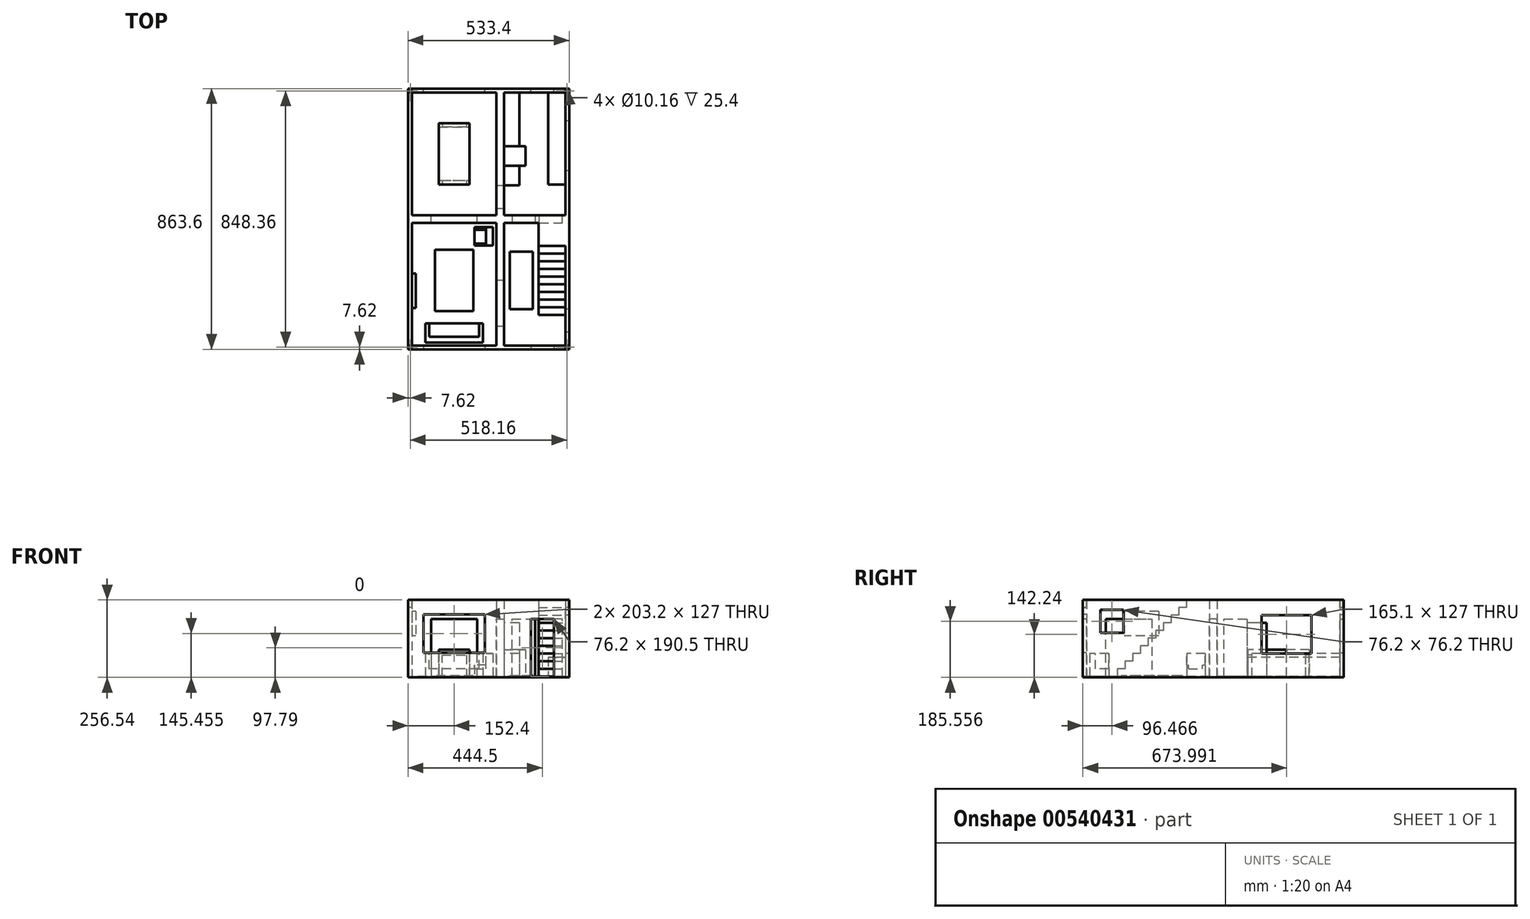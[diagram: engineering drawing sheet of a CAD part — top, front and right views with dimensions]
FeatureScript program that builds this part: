
annotation { "Feature Type Name" : "Feature", "Feature Type Description" : "" }
export const myFeature = defineFeature(function(context is Context, id is Id, definition is map)
    precondition{}
    {
        {
            var Q0;
            Q0=qCreatedBy(makeId("Top.planeOp"),FACE);
            var sketch = newSketch(context, id + "F0", { "sketchPlane" : qUnion([Q0])});
            skLineSegment(sketch, "E0.bottom", {"start": v(266.7, 431.8) * mm, "end": v(-266.7, 431.8) * mm});
            skLineSegment(sketch, "E0.top", {"start": v(266.7, -431.8) * mm, "end": v(-266.7, -431.8) * mm});
            skLineSegment(sketch, "E0.left", {"start": v(266.7, 431.8) * mm, "end": v(266.7, -431.8) * mm});
            skLineSegment(sketch, "E0.right", {"start": v(-266.7, 431.8) * mm, "end": v(-266.7, -431.8) * mm});
            skPoint(sketch, "E0.middle", {"position": v(0, 0) * mm});
            skSolve(sketch);
        }
        {
            var Q0;
            Q0=makeQuery(id+"F0.imprint","IMPRINT",FACE,{"disambiguationData":[TD([[makeQuery(id+"F0.imprint","IMPRINT",EDGE,{"derivedFrom":sQuery(id+"F0.wireOp",EDGE,"E0.bottom")}),1.0]])]});
            extrude(context, id + "F1", {"entities" : qUnion([Q0]), "depth" : 2.54 * mm, "offsetDistance" : 25.4 * mm});
        }
        {
            var Q0;
            Q0=makeQuery(id+"F1.opExtrude","CAP_FACE",FACE,{"disambiguationData":[OSD([sQuery(id+"F0.wireOp",EDGE,"E0.bottom"),sQuery(id+"F0.wireOp",EDGE,"E0.top"),sQuery(id+"F0.wireOp",EDGE,"E0.left"),sQuery(id+"F0.wireOp",EDGE,"E0.right")])],"isStart":false});
            var sketch = newSketch(context, id + "F2", { "sketchPlane" : qUnion([Q0])});
            skLineSegment(sketch, "E1.bottom", {"start": v(254, 419.1) * mm, "end": v(-254, 419.1) * mm});
            skLineSegment(sketch, "E1.top", {"start": v(254, -419.1) * mm, "end": v(-254, -419.1) * mm});
            skLineSegment(sketch, "E1.left", {"start": v(254, 419.1) * mm, "end": v(254, -419.1) * mm});
            skLineSegment(sketch, "E1.right", {"start": v(-254, 419.1) * mm, "end": v(-254, -419.1) * mm});
            skPoint(sketch, "E1.middle", {"position": v(0, 0) * mm});
            skSolve(sketch);
        }
        {
            var Q0;
            Q0=makeQuery(id+"F2.imprint","IMPRINT",FACE,{"disambiguationData":[TD([[makeQuery(id+"F2.imprint","IMPRINT",EDGE,{"derivedFrom":sQuery(id+"F2.wireOp",EDGE,"E1.bottom")}),-1.0]])]});
            extrude(context, id + "F3", {"entities" : qUnion([Q0]), "operationType" : NewBodyOperationType.ADD, "depth" : 254 * mm, "offsetDistance" : 25.4 * mm});
        }
        {
            var Q0;
            Q0=makeQuery(id+"F1.opExtrude","CAP_FACE",FACE,{"disambiguationData":[OSD([sQuery(id+"F0.wireOp",EDGE,"E0.bottom"),sQuery(id+"F0.wireOp",EDGE,"E0.top"),sQuery(id+"F0.wireOp",EDGE,"E0.left"),sQuery(id+"F0.wireOp",EDGE,"E0.right")])],"isStart":false});
            var sketch = newSketch(context, id + "F4", { "sketchPlane" : qUnion([Q0])});
            skLineSegment(sketch, "E2", {"start": v(50.8, 419.1) * mm, "end": v(50.8, -419.1) * mm});
            skLineSegment(sketch, "E3", {"start": v(50.8, 419.1) * mm, "end": v(25.4, 419.1) * mm});
            skLineSegment(sketch, "E4", {"start": v(25.4, 419.1) * mm, "end": v(25.4, -419.1) * mm});
            skLineSegment(sketch, "E5", {"start": v(25.4, -419.1) * mm, "end": v(50.8, -419.1) * mm});
            skLineSegment(sketch, "E6", {"start": v(254, -12.7) * mm, "end": v(254, 0) * mm});
            skLineSegment(sketch, "E7", {"start": v(-254, 0) * mm, "end": v(-254, -12.7) * mm});
            skLineSegment(sketch, "E8", {"start": v(254, -12.7) * mm, "end": v(-254, -12.7) * mm});
            skLineSegment(sketch, "E9", {"start": v(-254, 12.7) * mm, "end": v(254, 12.7) * mm});
            skSolve(sketch);
        }
        {
            var Q0;
            {var subQ0=sQuery(id+"F4.wireOp",EDGE,"E5");Q0=makeQuery(id+"F4.imprint","IMPRINT",FACE,{"disambiguationData":[TD([[makeQuery(id+"F4.imprint","IMPRINT",EDGE,{"derivedFrom":subQ0}),-1.0]])]});}
            var Q1;
            {var subQ0=sQuery(id+"F4.wireOp",EDGE,"E9");var subQ1=sQuery(id+"F4.wireOp",EDGE,"E2");var subQ2=makeQuery(id+"F4.imprint","INTERSECT",VERTEX,{"derivedFrom":[subQ1,subQ0]});Q1=makeQuery(id+"F4.imprint","IMPRINT",FACE,{"disambiguationData":[TD([[makeQuery(id+"F4.imprint","IMPRINT",EDGE,{"disambiguationData":[TD([[subQ2,-1.0]])],"derivedFrom":subQ1}),-1.0]])]});}
            var Q2;
            {var subQ6=sQuery(id+"F4.wireOp",EDGE,"E6");Q2=makeQuery(id+"F4.imprint","IMPRINT",FACE,{"disambiguationData":[TD([[makeQuery(id+"F4.imprint","IMPRINT",EDGE,{"derivedFrom":subQ6}),-1.0]])]});}
            var Q3;
            {var subQ6=sQuery(id+"F4.wireOp",EDGE,"E7");Q3=makeQuery(id+"F4.imprint","IMPRINT",FACE,{"disambiguationData":[TD([[makeQuery(id+"F4.imprint","IMPRINT",EDGE,{"derivedFrom":subQ6}),1.0]])]});}
            var Q4;
            {var subQ0=sQuery(id+"F4.wireOp",EDGE,"E3");Q4=makeQuery(id+"F4.imprint","IMPRINT",FACE,{"disambiguationData":[TD([[makeQuery(id+"F4.imprint","IMPRINT",EDGE,{"derivedFrom":subQ0}),1.0]])]});}
            extrude(context, id + "F5", {"entities" : qUnion([Q0, Q1, Q2, Q3, Q4]), "operationType" : NewBodyOperationType.ADD, "depth" : 254 * mm, "offsetDistance" : 25.4 * mm});
        }
        {
            var Q0;
            {var subQ0=sQuery(id+"F0.wireOp",EDGE,"E0.top");Q0=makeQuery(id+"F3.boolean.opBoolean","MERGE",FACE,{"derivedFrom":[makeQuery(id+"F1.opExtrude","SWEPT_FACE",FACE,{"disambiguationData":[OSD([subQ0])]}),makeQuery(id+"F3.opExtrude","SWEPT_FACE",FACE,{"disambiguationData":[OSD([subQ0])]})]});}
            var sketch = newSketch(context, id + "F6", { "sketchPlane" : qUnion([Q0])});
            skLineSegment(sketch, "E10", {"start": v(139.7, 193.04) * mm, "end": v(215.9, 193.04) * mm});
            skLineSegment(sketch, "E11", {"start": v(215.9, 193.04) * mm, "end": v(215.9, 2.54) * mm});
            skLineSegment(sketch, "E12", {"start": v(215.9, 2.54) * mm, "end": v(139.7, 2.54) * mm});
            skLineSegment(sketch, "E13", {"start": v(139.7, 2.54) * mm, "end": v(139.7, 193.04) * mm});
            skSolve(sketch);
        }
        {
            var Q0;
            Q0=makeQuery(id+"F6.imprint","IMPRINT",FACE,{"disambiguationData":[TD([[makeQuery(id+"F6.imprint","IMPRINT",EDGE,{"derivedFrom":sQuery(id+"F6.wireOp",EDGE,"E10")}),-1.0]])]});
            extrude(context, id + "F7", {"entities" : qUnion([Q0]), "operationType" : NewBodyOperationType.REMOVE, "oppositeDirection" : true, "depth" : 25.4 * mm, "offsetDistance" : 25.4 * mm});
        }
        {
            var Q0;
            {var subQ2=sQuery(id+"F4.wireOp",EDGE,"E8");var subQ3=sQuery(id+"F4.wireOp",EDGE,"E2");var subQ4=makeQuery(id+"F4.imprint","INTERSECT",VERTEX,{"derivedFrom":[subQ3,subQ2]});Q0=makeQuery(id+"F7.boolean.opBoolean","MERGE",FACE,{"derivedFrom":[makeQuery(id+"F5.boolean.opBoolean","SPLIT",FACE,{"disambiguationData":[TD([makeQuery(id+"F5.opExtrude","SWEPT_FACE",FACE,{"disambiguationData":[OSD([subQ3]),TDD([makeQuery(id+"F4.imprint","IMPRINT",EDGE,{"disambiguationData":[TD([[subQ4,-1.0]])],"derivedFrom":subQ3})])]})])],"derivedFrom":makeQuery(id+"F1.opExtrude","CAP_FACE",FACE,{"disambiguationData":[OSD([sQuery(id+"F0.wireOp",EDGE,"E0.bottom"),sQuery(id+"F0.wireOp",EDGE,"E0.top"),sQuery(id+"F0.wireOp",EDGE,"E0.left"),sQuery(id+"F0.wireOp",EDGE,"E0.right")])],"isStart":false})}),makeQuery(id+"F7.opExtrude","SWEPT_FACE",FACE,{"disambiguationData":[OSD([sQuery(id+"F6.wireOp",EDGE,"E12")])]})]});}
            var sketch = newSketch(context, id + "F8", { "sketchPlane" : qUnion([Q0])});
            skLineSegment(sketch, "E14", {"start": v(254, -12.7) * mm, "end": v(177.8, -12.7) * mm});
            skLineSegment(sketch, "E15", {"start": v(177.8, -12.7) * mm, "end": v(177.8, -317.5) * mm});
            skLineSegment(sketch, "E16", {"start": v(177.8, -317.5) * mm, "end": v(254, -317.5) * mm});
            skLineSegment(sketch, "E17", {"start": v(254, -12.7) * mm, "end": v(254, -317.5) * mm});
            skSolve(sketch);
        }
        {
            var Q0;
            Q0=makeQuery(id+"F8.imprint","IMPRINT",FACE,{"disambiguationData":[TD([[makeQuery(id+"F8.imprint","IMPRINT",EDGE,{"derivedFrom":sQuery(id+"F8.wireOp",EDGE,"E14")}),1.0]])]});
            extrude(context, id + "F9", {"entities" : qUnion([Q0]), "operationType" : NewBodyOperationType.ADD, "depth" : 25.4 * mm, "offsetDistance" : 25.4 * mm});
        }
        {
            var Q0;
            Q0=makeQuery(id+"F9.opExtrude","CAP_FACE",FACE,{"disambiguationData":[OSD([sQuery(id+"F8.wireOp",EDGE,"E14"),sQuery(id+"F8.wireOp",EDGE,"E15"),sQuery(id+"F8.wireOp",EDGE,"E16"),sQuery(id+"F8.wireOp",EDGE,"E17")])],"isStart":false});
            var sketch = newSketch(context, id + "F10", { "sketchPlane" : qUnion([Q0])});
            skLineSegment(sketch, "E18", {"start": v(177.8, -12.7) * mm, "end": v(177.8, -292.1) * mm});
            skLineSegment(sketch, "E19", {"start": v(177.8, -292.1) * mm, "end": v(254, -292.1) * mm});
            skLineSegment(sketch, "E20", {"start": v(254, -292.1) * mm, "end": v(254, -12.7) * mm});
            skLineSegment(sketch, "E21", {"start": v(254, -12.7) * mm, "end": v(177.8, -12.7) * mm});
            skSolve(sketch);
        }
        {
            var Q0;
            Q0 = qSketchRegion(id + "F10", true);
            extrude(context, id + "F11", {"entities" : qUnion([Q0]), "operationType" : NewBodyOperationType.ADD, "depth" : 25.4 * mm, "offsetDistance" : 25.4 * mm});
        }
        {
            var Q0;
            Q0=makeQuery(id+"F11.opExtrude","CAP_FACE",FACE,{"disambiguationData":[OSD([sQuery(id+"F10.wireOp",EDGE,"E18"),sQuery(id+"F10.wireOp",EDGE,"E19"),sQuery(id+"F10.wireOp",EDGE,"E20"),sQuery(id+"F10.wireOp",EDGE,"E21")])],"isStart":false});
            var sketch = newSketch(context, id + "F12", { "sketchPlane" : qUnion([Q0])});
            skLineSegment(sketch, "E22", {"start": v(177.8, -12.7) * mm, "end": v(177.8, -266.7) * mm});
            skLineSegment(sketch, "E23", {"start": v(177.8, -266.7) * mm, "end": v(254, -266.7) * mm});
            skLineSegment(sketch, "E24", {"start": v(254, -266.7) * mm, "end": v(254, -12.7) * mm});
            skLineSegment(sketch, "E25", {"start": v(254, -12.7) * mm, "end": v(177.8, -12.7) * mm});
            skSolve(sketch);
        }
        {
            var Q0;
            Q0 = qSketchRegion(id + "F12", true);
            extrude(context, id + "F13", {"entities" : qUnion([Q0]), "operationType" : NewBodyOperationType.ADD, "depth" : 25.4 * mm, "offsetDistance" : 25.4 * mm});
        }
        {
            var Q0;
            Q0=makeQuery(id+"F13.opExtrude","CAP_FACE",FACE,{"disambiguationData":[OSD([sQuery(id+"F12.wireOp",EDGE,"E22"),sQuery(id+"F12.wireOp",EDGE,"E23"),sQuery(id+"F12.wireOp",EDGE,"E24"),sQuery(id+"F12.wireOp",EDGE,"E25")])],"isStart":false});
            var sketch = newSketch(context, id + "F14", { "sketchPlane" : qUnion([Q0])});
            skLineSegment(sketch, "E26", {"start": v(177.8, -12.7) * mm, "end": v(177.8, -241.3) * mm});
            skLineSegment(sketch, "E27", {"start": v(177.8, -241.3) * mm, "end": v(254, -241.3) * mm});
            skLineSegment(sketch, "E28", {"start": v(254, -241.3) * mm, "end": v(254, -12.7) * mm});
            skLineSegment(sketch, "E29", {"start": v(254, -12.7) * mm, "end": v(177.8, -12.7) * mm});
            skSolve(sketch);
        }
        {
            var Q0;
            Q0 = qSketchRegion(id + "F14", true);
            extrude(context, id + "F15", {"entities" : qUnion([Q0]), "operationType" : NewBodyOperationType.ADD, "depth" : 25.4 * mm, "offsetDistance" : 25.4 * mm});
        }
        {
            var Q0;
            Q0=makeQuery(id+"F15.opExtrude","CAP_FACE",FACE,{"disambiguationData":[OSD([sQuery(id+"F14.wireOp",EDGE,"E26"),sQuery(id+"F14.wireOp",EDGE,"E27"),sQuery(id+"F14.wireOp",EDGE,"E28"),sQuery(id+"F14.wireOp",EDGE,"E29")])],"isStart":false});
            var sketch = newSketch(context, id + "F16", { "sketchPlane" : qUnion([Q0])});
            skLineSegment(sketch, "E30", {"start": v(177.8, -12.7) * mm, "end": v(177.8, -215.9) * mm});
            skLineSegment(sketch, "E31", {"start": v(177.8, -215.9) * mm, "end": v(254, -215.9) * mm});
            skLineSegment(sketch, "E32", {"start": v(254, -215.9) * mm, "end": v(254, -12.7) * mm});
            skLineSegment(sketch, "E33", {"start": v(254, -12.7) * mm, "end": v(177.8, -12.7) * mm});
            skSolve(sketch);
        }
        {
            var Q0;
            Q0 = qSketchRegion(id + "F16", true);
            extrude(context, id + "F17", {"entities" : qUnion([Q0]), "operationType" : NewBodyOperationType.ADD, "depth" : 25.4 * mm, "offsetDistance" : 25.4 * mm});
        }
        {
            var Q0;
            Q0=makeQuery(id+"F17.opExtrude","CAP_FACE",FACE,{"disambiguationData":[OSD([sQuery(id+"F16.wireOp",EDGE,"E30"),sQuery(id+"F16.wireOp",EDGE,"E31"),sQuery(id+"F16.wireOp",EDGE,"E32"),sQuery(id+"F16.wireOp",EDGE,"E33")])],"isStart":false});
            var sketch = newSketch(context, id + "F18", { "sketchPlane" : qUnion([Q0])});
            skLineSegment(sketch, "E34", {"start": v(177.8, -12.7) * mm, "end": v(177.8, -190.5) * mm});
            skLineSegment(sketch, "E35", {"start": v(177.8, -190.5) * mm, "end": v(254, -190.5) * mm});
            skLineSegment(sketch, "E36", {"start": v(254, -190.5) * mm, "end": v(254, -12.7) * mm});
            skLineSegment(sketch, "E37", {"start": v(254, -12.7) * mm, "end": v(177.8, -12.7) * mm});
            skSolve(sketch);
        }
        {
            var Q0;
            Q0 = qSketchRegion(id + "F18", true);
            extrude(context, id + "F19", {"entities" : qUnion([Q0]), "operationType" : NewBodyOperationType.ADD, "depth" : 25.4 * mm, "offsetDistance" : 25.4 * mm});
        }
        {
            var Q0;
            Q0=makeQuery(id+"F19.opExtrude","CAP_FACE",FACE,{"disambiguationData":[OSD([sQuery(id+"F18.wireOp",EDGE,"E34"),sQuery(id+"F18.wireOp",EDGE,"E35"),sQuery(id+"F18.wireOp",EDGE,"E36"),sQuery(id+"F18.wireOp",EDGE,"E37")])],"isStart":false});
            var sketch = newSketch(context, id + "F20", { "sketchPlane" : qUnion([Q0])});
            skLineSegment(sketch, "E38", {"start": v(177.8, -12.7) * mm, "end": v(177.8, -165.1) * mm});
            skLineSegment(sketch, "E39", {"start": v(177.8, -165.1) * mm, "end": v(254, -165.1) * mm});
            skLineSegment(sketch, "E40", {"start": v(254, -165.1) * mm, "end": v(254, -12.7) * mm});
            skLineSegment(sketch, "E41", {"start": v(254, -12.7) * mm, "end": v(177.8, -12.7) * mm});
            skSolve(sketch);
        }
        {
            var Q0;
            Q0 = qSketchRegion(id + "F20", true);
            extrude(context, id + "F21", {"entities" : qUnion([Q0]), "operationType" : NewBodyOperationType.ADD, "depth" : 25.4 * mm, "offsetDistance" : 25.4 * mm});
        }
        {
            var Q0;
            Q0=makeQuery(id+"F21.opExtrude","CAP_FACE",FACE,{"disambiguationData":[OSD([sQuery(id+"F20.wireOp",EDGE,"E38"),sQuery(id+"F20.wireOp",EDGE,"E39"),sQuery(id+"F20.wireOp",EDGE,"E40"),sQuery(id+"F20.wireOp",EDGE,"E41")])],"isStart":false});
            var sketch = newSketch(context, id + "F22", { "sketchPlane" : qUnion([Q0])});
            skLineSegment(sketch, "E42", {"start": v(177.8, -12.7) * mm, "end": v(177.8, -139.7) * mm});
            skLineSegment(sketch, "E43", {"start": v(177.8, -139.7) * mm, "end": v(254, -139.7) * mm});
            skLineSegment(sketch, "E44", {"start": v(254, -139.7) * mm, "end": v(254, -12.7) * mm});
            skLineSegment(sketch, "E45", {"start": v(254, -12.7) * mm, "end": v(177.8, -12.7) * mm});
            skSolve(sketch);
        }
        {
            var Q0;
            Q0=makeQuery(id+"F22.imprint","IMPRINT",FACE,{"disambiguationData":[TD([[makeQuery(id+"F22.imprint","IMPRINT",EDGE,{"derivedFrom":sQuery(id+"F22.wireOp",EDGE,"E42")}),1.0]])]});
            extrude(context, id + "F23", {"entities" : qUnion([Q0]), "operationType" : NewBodyOperationType.ADD, "depth" : 25.4 * mm, "offsetDistance" : 25.4 * mm});
        }
        {
            var Q0;
            Q0=makeQuery(id+"F23.opExtrude","CAP_FACE",FACE,{"disambiguationData":[OSD([sQuery(id+"F22.wireOp",EDGE,"E42"),sQuery(id+"F22.wireOp",EDGE,"E43"),sQuery(id+"F22.wireOp",EDGE,"E44"),sQuery(id+"F22.wireOp",EDGE,"E45")])],"isStart":false});
            var sketch = newSketch(context, id + "F24", { "sketchPlane" : qUnion([Q0])});
            skLineSegment(sketch, "E46", {"start": v(177.8, -12.7) * mm, "end": v(177.8, -114.3) * mm});
            skLineSegment(sketch, "E47", {"start": v(177.8, -114.3) * mm, "end": v(254, -114.3) * mm});
            skLineSegment(sketch, "E48", {"start": v(254, -114.3) * mm, "end": v(254, -12.7) * mm});
            skLineSegment(sketch, "E49", {"start": v(254, -12.7) * mm, "end": v(177.8, -12.7) * mm});
            skSolve(sketch);
        }
        {
            var Q0;
            Q0 = qSketchRegion(id + "F24", true);
            extrude(context, id + "F25", {"entities" : qUnion([Q0]), "operationType" : NewBodyOperationType.ADD, "depth" : 25.4 * mm, "offsetDistance" : 25.4 * mm});
        }
        {
            var Q0;
            Q0=makeQuery(id+"F25.opExtrude","CAP_FACE",FACE,{"disambiguationData":[OSD([sQuery(id+"F24.wireOp",EDGE,"E46"),sQuery(id+"F24.wireOp",EDGE,"E47"),sQuery(id+"F24.wireOp",EDGE,"E48"),sQuery(id+"F24.wireOp",EDGE,"E49")])],"isStart":false});
            var sketch = newSketch(context, id + "F26", { "sketchPlane" : qUnion([Q0])});
            skLineSegment(sketch, "E50", {"start": v(177.8, -12.7) * mm, "end": v(177.8, -88.9) * mm});
            skLineSegment(sketch, "E51", {"start": v(177.8, -88.9) * mm, "end": v(254, -88.9) * mm});
            skLineSegment(sketch, "E52", {"start": v(254, -88.9) * mm, "end": v(254, -12.7) * mm});
            skLineSegment(sketch, "E53", {"start": v(254, -12.7) * mm, "end": v(177.8, -12.7) * mm});
            skSolve(sketch);
        }
        {
            var Q0;
            Q0 = qSketchRegion(id + "F26", true);
            extrude(context, id + "F27", {"entities" : qUnion([Q0]), "operationType" : NewBodyOperationType.ADD, "depth" : 25.4 * mm, "offsetDistance" : 25.4 * mm});
        }
        {
            var Q0;
            {var subQ0=sQuery(id+"F4.wireOp",EDGE,"E8");Q0=makeQuery(id+"F5.opExtrude","SWEPT_FACE",FACE,{"disambiguationData":[OSD([subQ0]),TDD([makeQuery(id+"F4.imprint","IMPRINT",EDGE,{"disambiguationData":[TD([[makeQuery(id+"F4.imprint","INTERSECT",VERTEX,{"derivedFrom":[sQuery(id+"F4.wireOp",EDGE,"E2"),subQ0]}),1.0]])],"derivedFrom":subQ0})])]});}
            var sketch = newSketch(context, id + "F28", { "sketchPlane" : qUnion([Q0])});
            skLineSegment(sketch, "E54", {"start": v(77.55, 2.54) * mm, "end": v(77.55, 193.04) * mm});
            skLineSegment(sketch, "E55", {"start": v(77.55, 193.04) * mm, "end": v(153.75, 193.04) * mm});
            skLineSegment(sketch, "E56", {"start": v(153.75, 193.04) * mm, "end": v(153.75, 2.54) * mm});
            skLineSegment(sketch, "E57", {"start": v(153.75, 2.54) * mm, "end": v(77.55, 2.54) * mm});
            skSolve(sketch);
        }
        {
            var Q0;
            Q0=makeQuery(id+"F28.imprint","IMPRINT",FACE,{"disambiguationData":[TD([[makeQuery(id+"F28.imprint","IMPRINT",EDGE,{"derivedFrom":sQuery(id+"F28.wireOp",EDGE,"E54")}),-1.0]])]});
            extrude(context, id + "F29", {"entities" : qUnion([Q0]), "operationType" : NewBodyOperationType.REMOVE, "oppositeDirection" : true, "depth" : 25.4 * mm, "offsetDistance" : 25.4 * mm});
        }
        {
            var Q0;
            {var subQ0=sQuery(id+"F4.wireOp",EDGE,"E2");Q0=makeQuery(id+"F5.opExtrude","SWEPT_FACE",FACE,{"disambiguationData":[OSD([subQ0]),TDD([makeQuery(id+"F4.imprint","IMPRINT",EDGE,{"disambiguationData":[TD([[makeQuery(id+"F4.imprint","INTERSECT",VERTEX,{"derivedFrom":[subQ0,sQuery(id+"F4.wireOp",EDGE,"E9")]}),1.0]])],"derivedFrom":subQ0})])]});}
            var sketch = newSketch(context, id + "F30", { "sketchPlane" : qUnion([Q0])});
            skLineSegment(sketch, "E58", {"start": v(34.8, 2.54) * mm, "end": v(34.8, 193.04) * mm});
            skLineSegment(sketch, "E59", {"start": v(34.8, 193.04) * mm, "end": v(111, 193.04) * mm});
            skLineSegment(sketch, "E60", {"start": v(111, 193.04) * mm, "end": v(111, 2.54) * mm});
            skLineSegment(sketch, "E61", {"start": v(111, 2.54) * mm, "end": v(34.8, 2.54) * mm});
            skSolve(sketch);
        }
        {
            var Q0;
            Q0 = qSketchRegion(id + "F30", true);
            extrude(context, id + "F31", {"entities" : qUnion([Q0]), "operationType" : NewBodyOperationType.REMOVE, "oppositeDirection" : true, "depth" : 25.4 * mm, "offsetDistance" : 25.4 * mm});
        }
        {
            var Q0;
            {var subQ0=sQuery(id+"F4.wireOp",EDGE,"E9");Q0=makeQuery(id+"F5.opExtrude","SWEPT_FACE",FACE,{"disambiguationData":[OSD([subQ0]),TDD([makeQuery(id+"F4.imprint","IMPRINT",EDGE,{"disambiguationData":[TD([[makeQuery(id+"F4.imprint","INTERSECT",VERTEX,{"derivedFrom":[makeQuery(id+"F3.opExtrude","CAP_EDGE",EDGE,{"disambiguationData":[OSD([sQuery(id+"F2.wireOp",EDGE,"E1.right")])],"isStart":true}),subQ0]}),-1.0]])],"derivedFrom":subQ0})])]});}
            var sketch = newSketch(context, id + "F32", { "sketchPlane" : qUnion([Q0])});
            skLineSegment(sketch, "E62", {"start": v(38.1, 2.54) * mm, "end": v(38.1, 193.04) * mm});
            skLineSegment(sketch, "E63", {"start": v(38.1, 193.04) * mm, "end": v(190.5, 193.04) * mm});
            skLineSegment(sketch, "E64", {"start": v(190.5, 193.04) * mm, "end": v(190.5, 2.54) * mm});
            skLineSegment(sketch, "E65", {"start": v(190.5, 2.54) * mm, "end": v(38.1, 2.54) * mm});
            skSolve(sketch);
        }
        {
            var Q0;
            Q0 = qSketchRegion(id + "F32", true);
            extrude(context, id + "F33", {"entities" : qUnion([Q0]), "operationType" : NewBodyOperationType.REMOVE, "oppositeDirection" : true, "depth" : 25.4 * mm, "offsetDistance" : 25.4 * mm});
        }
        {
            var Q0;
            {var subQ0=sQuery(id+"F4.wireOp",EDGE,"E4");Q0=makeQuery(id+"F5.opExtrude","SWEPT_FACE",FACE,{"disambiguationData":[OSD([subQ0]),TDD([makeQuery(id+"F4.imprint","IMPRINT",EDGE,{"disambiguationData":[TD([[makeQuery(id+"F4.imprint","INTERSECT",VERTEX,{"derivedFrom":[subQ0,sQuery(id+"F4.wireOp",EDGE,"E8")]}),-1.0]])],"derivedFrom":subQ0})])]});}
            var sketch = newSketch(context, id + "F34", { "sketchPlane" : qUnion([Q0])});
            skLineSegment(sketch, "E66", {"start": v(355.6, 2.54) * mm, "end": v(355.6, 193.04) * mm});
            skLineSegment(sketch, "E67", {"start": v(355.6, 193.04) * mm, "end": v(203.2, 193.04) * mm});
            skLineSegment(sketch, "E68", {"start": v(203.2, 193.04) * mm, "end": v(203.2, 2.54) * mm});
            skPoint(sketch, "E68.endSnap0", {"position": v(215.9, 2.54) * mm});
            skLineSegment(sketch, "E69", {"start": v(203.2, 2.54) * mm, "end": v(355.6, 2.54) * mm});
            skSolve(sketch);
        }
        {
            var Q0;
            Q0 = qSketchRegion(id + "F34", true);
            extrude(context, id + "F35", {"entities" : qUnion([Q0]), "operationType" : NewBodyOperationType.REMOVE, "oppositeDirection" : true, "depth" : 25.4 * mm, "offsetDistance" : 25.4 * mm});
        }
        {
            var Q0;
            {var subQ0=sQuery(id+"F2.wireOp",EDGE,"E1.right");var subQ1=sQuery(id+"F2.wireOp",EDGE,"E1.left");Q0=makeQuery(id+"F27.boolean.opBoolean","MERGE",FACE,{"derivedFrom":[makeQuery(id+"F5.boolean.opBoolean","MERGE",FACE,{"derivedFrom":[makeQuery(id+"F3.opExtrude","CAP_FACE",FACE,{"disambiguationData":[OSD([sQuery(id+"F0.wireOp",EDGE,"E0.bottom"),sQuery(id+"F0.wireOp",EDGE,"E0.top"),sQuery(id+"F0.wireOp",EDGE,"E0.left"),sQuery(id+"F0.wireOp",EDGE,"E0.right"),sQuery(id+"F2.wireOp",EDGE,"E1.bottom"),sQuery(id+"F2.wireOp",EDGE,"E1.top"),subQ1,subQ0])],"isStart":false}),makeQuery(id+"F5.opExtrude","CAP_FACE",FACE,{"disambiguationData":[OSD([subQ1,subQ0,sQuery(id+"F4.wireOp",EDGE,"E2"),sQuery(id+"F4.wireOp",EDGE,"E3"),sQuery(id+"F4.wireOp",EDGE,"E4"),sQuery(id+"F4.wireOp",EDGE,"E5"),sQuery(id+"F4.wireOp",EDGE,"E6"),sQuery(id+"F4.wireOp",EDGE,"E7"),sQuery(id+"F4.wireOp",EDGE,"E8"),sQuery(id+"F4.wireOp",EDGE,"E9")])],"isStart":false})]}),makeQuery(id+"F27.opExtrude","CAP_FACE",FACE,{"disambiguationData":[OSD([sQuery(id+"F26.wireOp",EDGE,"E50"),sQuery(id+"F26.wireOp",EDGE,"E51"),sQuery(id+"F26.wireOp",EDGE,"E52"),sQuery(id+"F26.wireOp",EDGE,"E53")])],"isStart":false})]});}
            var sketch = newSketch(context, id + "F36", { "sketchPlane" : qUnion([Q0])});
            skLineSegment(sketch, "E70.0", {"start": v(177.8, -88.9) * mm, "end": v(254, -88.9) * mm});
            skLineSegment(sketch, "E71.0", {"start": v(254, -419.1) * mm, "end": v(50.8, -419.1) * mm});
            skLineSegment(sketch, "E72", {"start": v(177.8, -88.9) * mm, "end": v(177.8, -12.7) * mm});
            skLineSegment(sketch, "E73", {"start": v(254, -12.7) * mm, "end": v(254, -88.9) * mm});
            skLineSegment(sketch, "E74", {"start": v(177.8, -12.7) * mm, "end": v(254, -12.7) * mm});
            skSolve(sketch);
        }
        {
            var Q0;
            {var subQ0=sQuery(id+"F0.wireOp",EDGE,"E0.left");Q0=makeQuery(id+"F3.boolean.opBoolean","MERGE",FACE,{"derivedFrom":[makeQuery(id+"F1.opExtrude","SWEPT_FACE",FACE,{"disambiguationData":[OSD([subQ0])]}),makeQuery(id+"F3.opExtrude","SWEPT_FACE",FACE,{"disambiguationData":[OSD([subQ0])]})]});}
            var sketch = newSketch(context, id + "F37", { "sketchPlane" : qUnion([Q0])});
            skLineSegment(sketch, "E75", {"start": v(-373.43, 223.66) * mm, "end": v(-373.43, 147.46) * mm});
            skLineSegment(sketch, "E76", {"start": v(-373.43, 147.46) * mm, "end": v(-297.23, 147.46) * mm});
            skLineSegment(sketch, "E77", {"start": v(-297.23, 147.46) * mm, "end": v(-297.23, 223.66) * mm});
            skLineSegment(sketch, "E78", {"start": v(-297.23, 223.66) * mm, "end": v(-373.43, 223.66) * mm});
            skSolve(sketch);
        }
        {
            var Q0;
            Q0=makeQuery(id+"F37.imprint","IMPRINT",FACE,{"disambiguationData":[TD([[makeQuery(id+"F37.imprint","IMPRINT",EDGE,{"derivedFrom":sQuery(id+"F37.wireOp",EDGE,"E75")}),1.0]])]});
            extrude(context, id + "F38", {"entities" : qUnion([Q0]), "operationType" : NewBodyOperationType.REMOVE, "oppositeDirection" : true, "depth" : 25.4 * mm, "offsetDistance" : 25.4 * mm});
        }
        {
            var Q0;
            {var subQ0=sQuery(id+"F0.wireOp",EDGE,"E0.top");Q0=makeQuery(id+"F3.boolean.opBoolean","MERGE",FACE,{"derivedFrom":[makeQuery(id+"F1.opExtrude","SWEPT_FACE",FACE,{"disambiguationData":[OSD([subQ0])]}),makeQuery(id+"F3.opExtrude","SWEPT_FACE",FACE,{"disambiguationData":[OSD([subQ0])]})]});}
            var sketch = newSketch(context, id + "F39", { "sketchPlane" : qUnion([Q0])});
            skLineSegment(sketch, "E79", {"start": v(-12.7, 81.95) * mm, "end": v(-215.9, 81.95) * mm});
            skLineSegment(sketch, "E80", {"start": v(-215.9, 81.95) * mm, "end": v(-215.9, 208.95) * mm});
            skLineSegment(sketch, "E81", {"start": v(-215.9, 208.95) * mm, "end": v(-12.7, 208.95) * mm});
            skLineSegment(sketch, "E82", {"start": v(-12.7, 208.95) * mm, "end": v(-12.7, 81.95) * mm});
            skSolve(sketch);
        }
        {
            var Q0;
            Q0=makeQuery(id+"F39.imprint","IMPRINT",FACE,{"disambiguationData":[TD([[makeQuery(id+"F39.imprint","IMPRINT",EDGE,{"derivedFrom":sQuery(id+"F39.wireOp",EDGE,"E79")}),-1.0]])]});
            extrude(context, id + "F40", {"entities" : qUnion([Q0]), "operationType" : NewBodyOperationType.REMOVE, "oppositeDirection" : true, "depth" : 25.4 * mm, "offsetDistance" : 25.4 * mm});
        }
        {
            var Q0;
            {var subQ0=sQuery(id+"F0.wireOp",EDGE,"E0.bottom");Q0=makeQuery(id+"F3.boolean.opBoolean","MERGE",FACE,{"derivedFrom":[makeQuery(id+"F1.opExtrude","SWEPT_FACE",FACE,{"disambiguationData":[OSD([subQ0])]}),makeQuery(id+"F3.opExtrude","SWEPT_FACE",FACE,{"disambiguationData":[OSD([subQ0])]})]});}
            var sketch = newSketch(context, id + "F41", { "sketchPlane" : qUnion([Q0])});
            skLineSegment(sketch, "E83.0", {"start": v(215.9, 208.95) * mm, "end": v(12.7, 208.95) * mm});
            skLineSegment(sketch, "E83.1", {"start": v(215.9, 81.95) * mm, "end": v(215.9, 208.95) * mm});
            skLineSegment(sketch, "E83.2", {"start": v(12.7, 81.95) * mm, "end": v(215.9, 81.95) * mm});
            skLineSegment(sketch, "E83.3", {"start": v(12.7, 208.95) * mm, "end": v(12.7, 81.95) * mm});
            skSolve(sketch);
        }
        {
            var Q0;
            Q0 = qSketchRegion(id + "F41", true);
            extrude(context, id + "F42", {"entities" : qUnion([Q0]), "operationType" : NewBodyOperationType.REMOVE, "oppositeDirection" : true, "depth" : 25.4 * mm, "offsetDistance" : 25.4 * mm});
        }
        {
            var Q0;
            {var subQ0=sQuery(id+"F0.wireOp",EDGE,"E0.bottom");Q0=makeQuery(id+"F3.boolean.opBoolean","MERGE",FACE,{"derivedFrom":[makeQuery(id+"F1.opExtrude","SWEPT_FACE",FACE,{"disambiguationData":[OSD([subQ0])]}),makeQuery(id+"F3.opExtrude","SWEPT_FACE",FACE,{"disambiguationData":[OSD([subQ0])]})]});}
            var sketch = newSketch(context, id + "F43", { "sketchPlane" : qUnion([Q0])});
            skLineSegment(sketch, "E84.0", {"start": v(-215.9, 193.04) * mm, "end": v(-215.9, 2.54) * mm});
            skLineSegment(sketch, "E85.0", {"start": v(-139.7, 193.04) * mm, "end": v(-215.9, 193.04) * mm});
            skLineSegment(sketch, "E86.0", {"start": v(-139.7, 2.54) * mm, "end": v(-139.7, 193.04) * mm});
            skLineSegment(sketch, "E87.0", {"start": v(-215.9, 2.54) * mm, "end": v(-139.7, 2.54) * mm});
            skSolve(sketch);
        }
        {
            var Q0;
            Q0=makeQuery(id+"F43.imprint","IMPRINT",FACE,{"disambiguationData":[TD([[makeQuery(id+"F43.imprint","IMPRINT",EDGE,{"derivedFrom":sQuery(id+"F43.wireOp",EDGE,"E84.0")}),1.0]])]});
            extrude(context, id + "F44", {"entities" : qUnion([Q0]), "operationType" : NewBodyOperationType.REMOVE, "oppositeDirection" : true, "depth" : 25.4 * mm, "offsetDistance" : 25.4 * mm});
        }
        {
            var Q0;
            {var subQ0=sQuery(id+"F4.wireOp",EDGE,"E9");Q0=makeQuery(id+"F5.opExtrude","SWEPT_FACE",FACE,{"disambiguationData":[OSD([subQ0]),TDD([makeQuery(id+"F4.imprint","IMPRINT",EDGE,{"disambiguationData":[TD([[makeQuery(id+"F4.imprint","INTERSECT",VERTEX,{"derivedFrom":[makeQuery(id+"F3.opExtrude","CAP_EDGE",EDGE,{"disambiguationData":[OSD([sQuery(id+"F2.wireOp",EDGE,"E1.left")])],"isStart":true}),subQ0]}),1.0]])],"derivedFrom":subQ0})])]});}
            var sketch = newSketch(context, id + "F45", { "sketchPlane" : qUnion([Q0])});
            skLineSegment(sketch, "E88", {"start": v(-244.8, 2.54) * mm, "end": v(-244.8, 193.04) * mm});
            skLineSegment(sketch, "E89", {"start": v(-244.8, 193.04) * mm, "end": v(-168.6, 193.04) * mm});
            skLineSegment(sketch, "E90", {"start": v(-168.6, 193.04) * mm, "end": v(-168.6, 2.54) * mm});
            skLineSegment(sketch, "E91", {"start": v(-168.6, 2.54) * mm, "end": v(-244.8, 2.54) * mm});
            skSolve(sketch);
        }
        {
            var Q0;
            Q0 = qSketchRegion(id + "F45", true);
            extrude(context, id + "F46", {"entities" : qUnion([Q0]), "operationType" : NewBodyOperationType.REMOVE, "oppositeDirection" : true, "depth" : 25.4 * mm, "offsetDistance" : 25.4 * mm});
        }
        {
            var Q0;
            Q0=makeQuery(id+"F27.boolean.opBoolean","MERGE",FACE,{"derivedFrom":[makeQuery(id+"F25.boolean.opBoolean","MERGE",FACE,{"derivedFrom":[makeQuery(id+"F23.boolean.opBoolean","MERGE",FACE,{"derivedFrom":[makeQuery(id+"F21.boolean.opBoolean","MERGE",FACE,{"derivedFrom":[makeQuery(id+"F19.boolean.opBoolean","MERGE",FACE,{"derivedFrom":[makeQuery(id+"F17.boolean.opBoolean","MERGE",FACE,{"derivedFrom":[makeQuery(id+"F15.boolean.opBoolean","MERGE",FACE,{"derivedFrom":[makeQuery(id+"F13.boolean.opBoolean","MERGE",FACE,{"derivedFrom":[makeQuery(id+"F11.boolean.opBoolean","MERGE",FACE,{"derivedFrom":[makeQuery(id+"F9.opExtrude","SWEPT_FACE",FACE,{"disambiguationData":[OSD([sQuery(id+"F8.wireOp",EDGE,"E15")])]}),makeQuery(id+"F11.opExtrude","SWEPT_FACE",FACE,{"disambiguationData":[OSD([sQuery(id+"F10.wireOp",EDGE,"E18")])]})]}),makeQuery(id+"F13.opExtrude","SWEPT_FACE",FACE,{"disambiguationData":[OSD([sQuery(id+"F12.wireOp",EDGE,"E22")])]})]}),makeQuery(id+"F15.opExtrude","SWEPT_FACE",FACE,{"disambiguationData":[OSD([sQuery(id+"F14.wireOp",EDGE,"E26")])]})]}),makeQuery(id+"F17.opExtrude","SWEPT_FACE",FACE,{"disambiguationData":[OSD([sQuery(id+"F16.wireOp",EDGE,"E30")])]})]}),makeQuery(id+"F19.opExtrude","SWEPT_FACE",FACE,{"disambiguationData":[OSD([sQuery(id+"F18.wireOp",EDGE,"E34")])]})]}),makeQuery(id+"F21.opExtrude","SWEPT_FACE",FACE,{"disambiguationData":[OSD([sQuery(id+"F20.wireOp",EDGE,"E38")])]})]}),makeQuery(id+"F23.opExtrude","SWEPT_FACE",FACE,{"disambiguationData":[OSD([sQuery(id+"F22.wireOp",EDGE,"E42")])]})]}),makeQuery(id+"F25.opExtrude","SWEPT_FACE",FACE,{"disambiguationData":[OSD([sQuery(id+"F24.wireOp",EDGE,"E46")])]})]}),makeQuery(id+"F27.opExtrude","SWEPT_FACE",FACE,{"disambiguationData":[OSD([sQuery(id+"F26.wireOp",EDGE,"E50")])]})]});
            var sketch = newSketch(context, id + "F47", { "sketchPlane" : qUnion([Q0])});
            skLineSegment(sketch, "E92.0", {"start": v(88.9, 256.54) * mm, "end": v(12.7, 256.54) * mm});
            skLineSegment(sketch, "E93.0", {"start": v(88.9, 256.54) * mm, "end": v(88.9, 231.14) * mm});
            skLineSegment(sketch, "E94.0", {"start": v(88.9, 231.14) * mm, "end": v(114.3, 231.14) * mm});
            skLineSegment(sketch, "E95.0", {"start": v(114.3, 231.14) * mm, "end": v(114.3, 205.74) * mm});
            skLineSegment(sketch, "E96.0", {"start": v(114.3, 205.74) * mm, "end": v(139.7, 205.74) * mm});
            skLineSegment(sketch, "E97.0", {"start": v(139.7, 205.74) * mm, "end": v(139.7, 180.34) * mm});
            skLineSegment(sketch, "E98.0", {"start": v(139.7, 180.34) * mm, "end": v(165.1, 180.34) * mm});
            skLineSegment(sketch, "E99.0", {"start": v(165.1, 180.34) * mm, "end": v(165.1, 154.94) * mm});
            skLineSegment(sketch, "E100.0", {"start": v(165.1, 154.94) * mm, "end": v(190.5, 154.94) * mm});
            skLineSegment(sketch, "E101.0", {"start": v(190.5, 154.94) * mm, "end": v(190.5, 129.54) * mm});
            skLineSegment(sketch, "E102.0", {"start": v(190.5, 129.54) * mm, "end": v(215.9, 129.54) * mm});
            skLineSegment(sketch, "E103.0", {"start": v(215.9, 129.54) * mm, "end": v(215.9, 104.14) * mm});
            skLineSegment(sketch, "E104.0", {"start": v(215.9, 104.14) * mm, "end": v(241.3, 104.14) * mm});
            skLineSegment(sketch, "E105.0", {"start": v(241.3, 104.14) * mm, "end": v(241.3, 78.74) * mm});
            skLineSegment(sketch, "E106.0", {"start": v(241.3, 78.74) * mm, "end": v(266.7, 78.74) * mm});
            skLineSegment(sketch, "E107.0", {"start": v(266.7, 78.74) * mm, "end": v(266.7, 53.34) * mm});
            skLineSegment(sketch, "E108.0", {"start": v(266.7, 53.34) * mm, "end": v(292.1, 53.34) * mm});
            skLineSegment(sketch, "E109.0", {"start": v(292.1, 53.34) * mm, "end": v(292.1, 27.94) * mm});
            skLineSegment(sketch, "E110.0", {"start": v(292.1, 27.94) * mm, "end": v(317.5, 27.94) * mm});
            skLineSegment(sketch, "E111.0", {"start": v(317.5, 27.94) * mm, "end": v(317.5, 2.54) * mm});
            skLineSegment(sketch, "E112.0", {"start": v(12.7, 2.54) * mm, "end": v(317.5, 2.54) * mm});
            skLineSegment(sketch, "E113.0", {"start": v(12.7, 193.04) * mm, "end": v(12.7, 2.54) * mm});
            skLineSegment(sketch, "E114.0", {"start": v(12.7, 256.54) * mm, "end": v(12.7, 193.04) * mm});
            skSolve(sketch);
        }
        {
            var Q0;
            Q0 = qSketchRegion(id + "F47", true);
            extrude(context, id + "F48", {"entities" : qUnion([Q0]), "operationType" : NewBodyOperationType.ADD, "depth" : 12.7 * mm, "offsetDistance" : 25.4 * mm});
        }
        {
            var Q0;
            {var subQ3=sQuery(id+"F2.wireOp",EDGE,"E1.left");var subQ4=sQuery(id+"F2.wireOp",EDGE,"E1.bottom");Q0=makeQuery(id+"F5.boolean.opBoolean","SPLIT",FACE,{"disambiguationData":[TD([makeQuery(id+"F3.opExtrude","SWEPT_FACE",FACE,{"disambiguationData":[OSD([subQ4])]})])],"derivedFrom":makeQuery(id+"F3.opExtrude","SWEPT_FACE",FACE,{"disambiguationData":[OSD([subQ3])]})});}
            var sketch = newSketch(context, id + "F49", { "sketchPlane" : qUnion([Q0])});
            skLineSegment(sketch, "E115", {"start": v(-324.74, 205.74) * mm, "end": v(-324.74, 78.74) * mm});
            skLineSegment(sketch, "E116", {"start": v(-324.74, 78.74) * mm, "end": v(-159.64, 78.74) * mm});
            skLineSegment(sketch, "E117", {"start": v(-159.64, 78.74) * mm, "end": v(-159.64, 205.74) * mm});
            skLineSegment(sketch, "E118", {"start": v(-159.64, 205.74) * mm, "end": v(-324.74, 205.74) * mm});
            skLineSegment(sketch, "E119.0", {"start": v(-419.1, 2.54) * mm, "end": v(-12.7, 2.54) * mm});
            skSolve(sketch);
        }
        {
            var Q0;
            Q0 = qSketchRegion(id + "F49", true);
            extrude(context, id + "F50", {"entities" : qUnion([Q0]), "operationType" : NewBodyOperationType.REMOVE, "oppositeDirection" : true, "depth" : 25.4 * mm, "offsetDistance" : 25.4 * mm});
        }
        {
            var Q0;
            Q0=makeQuery(id+"F36.imprint","IMPRINT",FACE,{"disambiguationData":[TD([[makeQuery(id+"F36.imprint","IMPRINT",EDGE,{"derivedFrom":sQuery(id+"F36.wireOp",EDGE,"E71.0")}),1.0]])]});
            var sketch = newSketch(context, id + "F51", { "sketchPlane" : qUnion([Q0])});
            skCircle(sketch, "E120", {"center": v(259.08, -424.18) * mm, "radius": 5.08 * mm});
            skCircle(sketch, "E121", {"center": v(-259.08, -424.18) * mm, "radius": 5.08 * mm});
            skCircle(sketch, "E122", {"center": v(-259.08, 424.18) * mm, "radius": 5.08 * mm});
            skCircle(sketch, "E123", {"center": v(259.08, 424.18) * mm, "radius": 5.08 * mm});
            skSolve(sketch);
        }
        {
            var Q0;
            Q0 = qSketchRegion(id + "F51", true);
            extrude(context, id + "F52", {"entities" : qUnion([Q0]), "operationType" : NewBodyOperationType.REMOVE, "oppositeDirection" : true, "depth" : 25.4 * mm, "offsetDistance" : 25.4 * mm});
        }
        {
            var Q0;
            {var subQ2=sQuery(id+"F2.wireOp",EDGE,"E1.left");var subQ4=sQuery(id+"F4.wireOp",EDGE,"E8");var subQ5=makeQuery(id+"F3.opExtrude","CAP_EDGE",EDGE,{"disambiguationData":[OSD([subQ2])],"isStart":true});var subQ6=sQuery(id+"F4.wireOp",EDGE,"E2");var subQ7=makeQuery(id+"F4.imprint","INTERSECT",VERTEX,{"derivedFrom":[subQ6,subQ4]});var subQ10=makeQuery(id+"F1.opExtrude","CAP_FACE",FACE,{"disambiguationData":[OSD([sQuery(id+"F0.wireOp",EDGE,"E0.bottom"),sQuery(id+"F0.wireOp",EDGE,"E0.top"),sQuery(id+"F0.wireOp",EDGE,"E0.left"),sQuery(id+"F0.wireOp",EDGE,"E0.right")])],"isStart":false});var subQ15=sQuery(id+"F4.wireOp",EDGE,"E9");var subQ17=sQuery(id+"F2.wireOp",EDGE,"E1.right");var subQ19=sQuery(id+"F4.wireOp",EDGE,"E4");var subQ21=makeQuery(id+"F3.opExtrude","CAP_EDGE",EDGE,{"disambiguationData":[OSD([subQ17])],"isStart":true});var subQ22=makeQuery(id+"F4.imprint","INTERSECT",VERTEX,{"derivedFrom":[subQ19,subQ4]});Q0=makeQuery(id+"F46.boolean.opBoolean","MERGE",FACE,{"derivedFrom":[makeQuery(id+"F44.boolean.opBoolean","MERGE",FACE,{"derivedFrom":[makeQuery(id+"F35.boolean.opBoolean","MERGE",FACE,{"derivedFrom":[makeQuery(id+"F33.boolean.opBoolean","MERGE",FACE,{"derivedFrom":[makeQuery(id+"F5.boolean.opBoolean","SPLIT",FACE,{"disambiguationData":[TD([makeQuery(id+"F5.opExtrude","SWEPT_FACE",FACE,{"disambiguationData":[OSD([subQ19]),TDD([makeQuery(id+"F4.imprint","IMPRINT",EDGE,{"disambiguationData":[TD([[subQ22,-1.0]])],"derivedFrom":subQ19})])]})])],"derivedFrom":subQ10}),makeQuery(id+"F31.boolean.opBoolean","MERGE",FACE,{"derivedFrom":[makeQuery(id+"F5.boolean.opBoolean","SPLIT",FACE,{"disambiguationData":[TD([makeQuery(id+"F5.opExtrude","SWEPT_FACE",FACE,{"disambiguationData":[OSD([subQ15]),TDD([makeQuery(id+"F4.imprint","IMPRINT",EDGE,{"disambiguationData":[TD([[makeQuery(id+"F4.imprint","INTERSECT",VERTEX,{"derivedFrom":[subQ21,subQ15]}),-1.0]])],"derivedFrom":subQ15})])]})])],"derivedFrom":subQ10}),makeQuery(id+"F29.boolean.opBoolean","MERGE",FACE,{"derivedFrom":[makeQuery(id+"F5.boolean.opBoolean","SPLIT",FACE,{"disambiguationData":[TD([makeQuery(id+"F5.opExtrude","SWEPT_FACE",FACE,{"disambiguationData":[OSD([subQ15]),TDD([makeQuery(id+"F4.imprint","IMPRINT",EDGE,{"disambiguationData":[TD([[makeQuery(id+"F4.imprint","INTERSECT",VERTEX,{"derivedFrom":[subQ5,subQ15]}),1.0]])],"derivedFrom":subQ15})])]})])],"derivedFrom":subQ10}),makeQuery(id+"F7.boolean.opBoolean","MERGE",FACE,{"derivedFrom":[makeQuery(id+"F5.boolean.opBoolean","SPLIT",FACE,{"disambiguationData":[TD([makeQuery(id+"F5.opExtrude","SWEPT_FACE",FACE,{"disambiguationData":[OSD([subQ6]),TDD([makeQuery(id+"F4.imprint","IMPRINT",EDGE,{"disambiguationData":[TD([[subQ7,-1.0]])],"derivedFrom":subQ6})])]})])],"derivedFrom":subQ10}),makeQuery(id+"F7.opExtrude","SWEPT_FACE",FACE,{"disambiguationData":[OSD([sQuery(id+"F6.wireOp",EDGE,"E12")])]})]}),makeQuery(id+"F29.opExtrude","SWEPT_FACE",FACE,{"disambiguationData":[OSD([sQuery(id+"F28.wireOp",EDGE,"E57")])]})]}),makeQuery(id+"F31.opExtrude","SWEPT_FACE",FACE,{"disambiguationData":[OSD([sQuery(id+"F30.wireOp",EDGE,"E61")])]})]}),makeQuery(id+"F33.opExtrude","SWEPT_FACE",FACE,{"disambiguationData":[OSD([sQuery(id+"F32.wireOp",EDGE,"E65")])]})]}),makeQuery(id+"F35.opExtrude","SWEPT_FACE",FACE,{"disambiguationData":[OSD([sQuery(id+"F34.wireOp",EDGE,"E69")])]})]}),makeQuery(id+"F44.opExtrude","SWEPT_FACE",FACE,{"disambiguationData":[OSD([sQuery(id+"F43.wireOp",EDGE,"E87.0")])]})]}),makeQuery(id+"F46.opExtrude","SWEPT_FACE",FACE,{"disambiguationData":[OSD([sQuery(id+"F45.wireOp",EDGE,"E91")])]})]});}
            var sketch = newSketch(context, id + "F53", { "sketchPlane" : qUnion([Q0])});
            skLineSegment(sketch, "E124.bottom", {"start": v(-18.88, -346.07) * mm, "end": v(-209.38, -346.07) * mm});
            skLineSegment(sketch, "E124.top", {"start": v(-18.88, -409.57) * mm, "end": v(-209.38, -409.57) * mm});
            skLineSegment(sketch, "E124.left", {"start": v(-18.88, -346.07) * mm, "end": v(-18.88, -409.57) * mm});
            skLineSegment(sketch, "E124.right", {"start": v(-209.38, -346.07) * mm, "end": v(-209.38, -409.57) * mm});
            skPoint(sketch, "E124.middle", {"position": v(-114.13, -377.82) * mm});
            skSolve(sketch);
        }
        {
            var Q0;
            Q0 = qSketchRegion(id + "F53", true);
            extrude(context, id + "F54", {"entities" : qUnion([Q0]), "operationType" : NewBodyOperationType.ADD, "depth" : 76.2 * mm, "offsetDistance" : 25.4 * mm});
        }
        {
            var Q0;
            Q0=makeQuery(id+"F54.opExtrude","CAP_FACE",FACE,{"disambiguationData":[OSD([sQuery(id+"F53.wireOp",EDGE,"E124.bottom"),sQuery(id+"F53.wireOp",EDGE,"E124.top"),sQuery(id+"F53.wireOp",EDGE,"E124.left"),sQuery(id+"F53.wireOp",EDGE,"E124.right")])],"isStart":false});
            var sketch = newSketch(context, id + "F55", { "sketchPlane" : qUnion([Q0])});
            skLineSegment(sketch, "E125.bottom", {"start": v(-31.58, -346.07) * mm, "end": v(-196.68, -346.07) * mm});
            skLineSegment(sketch, "E125.top", {"start": v(-31.58, -390.52) * mm, "end": v(-196.68, -390.52) * mm});
            skLineSegment(sketch, "E125.left", {"start": v(-31.58, -346.07) * mm, "end": v(-31.58, -390.52) * mm});
            skLineSegment(sketch, "E125.right", {"start": v(-196.68, -346.07) * mm, "end": v(-196.68, -390.52) * mm});
            skPoint(sketch, "E125.middle", {"position": v(-114.13, -368.3) * mm});
            skPoint(sketch, "E125.middle.positionSnap0", {"position": v(-114.13, -346.07) * mm});
            skPoint(sketch, "E125.centerSnap0", {"position": v(-114.13, -346.07) * mm});
            skSolve(sketch);
        }
        {
            var Q0;
            Q0 = qSketchRegion(id + "F55", true);
            extrude(context, id + "F56", {"entities" : qUnion([Q0]), "operationType" : NewBodyOperationType.REMOVE, "oppositeDirection" : true, "depth" : 50.8 * mm, "offsetDistance" : 25.4 * mm});
        }
        {
            var Q0;
            {var subQ2=sQuery(id+"F2.wireOp",EDGE,"E1.left");var subQ4=sQuery(id+"F4.wireOp",EDGE,"E8");var subQ5=makeQuery(id+"F3.opExtrude","CAP_EDGE",EDGE,{"disambiguationData":[OSD([subQ2])],"isStart":true});var subQ6=sQuery(id+"F4.wireOp",EDGE,"E2");var subQ7=makeQuery(id+"F4.imprint","INTERSECT",VERTEX,{"derivedFrom":[subQ6,subQ4]});var subQ10=makeQuery(id+"F1.opExtrude","CAP_FACE",FACE,{"disambiguationData":[OSD([sQuery(id+"F0.wireOp",EDGE,"E0.bottom"),sQuery(id+"F0.wireOp",EDGE,"E0.top"),sQuery(id+"F0.wireOp",EDGE,"E0.left"),sQuery(id+"F0.wireOp",EDGE,"E0.right")])],"isStart":false});var subQ15=sQuery(id+"F4.wireOp",EDGE,"E9");var subQ17=sQuery(id+"F2.wireOp",EDGE,"E1.right");var subQ19=sQuery(id+"F4.wireOp",EDGE,"E4");var subQ21=makeQuery(id+"F3.opExtrude","CAP_EDGE",EDGE,{"disambiguationData":[OSD([subQ17])],"isStart":true});var subQ22=makeQuery(id+"F4.imprint","INTERSECT",VERTEX,{"derivedFrom":[subQ19,subQ4]});Q0=makeQuery(id+"F46.boolean.opBoolean","MERGE",FACE,{"derivedFrom":[makeQuery(id+"F44.boolean.opBoolean","MERGE",FACE,{"derivedFrom":[makeQuery(id+"F35.boolean.opBoolean","MERGE",FACE,{"derivedFrom":[makeQuery(id+"F33.boolean.opBoolean","MERGE",FACE,{"derivedFrom":[makeQuery(id+"F5.boolean.opBoolean","SPLIT",FACE,{"disambiguationData":[TD([makeQuery(id+"F5.opExtrude","SWEPT_FACE",FACE,{"disambiguationData":[OSD([subQ19]),TDD([makeQuery(id+"F4.imprint","IMPRINT",EDGE,{"disambiguationData":[TD([[subQ22,-1.0]])],"derivedFrom":subQ19})])]})])],"derivedFrom":subQ10}),makeQuery(id+"F31.boolean.opBoolean","MERGE",FACE,{"derivedFrom":[makeQuery(id+"F5.boolean.opBoolean","SPLIT",FACE,{"disambiguationData":[TD([makeQuery(id+"F5.opExtrude","SWEPT_FACE",FACE,{"disambiguationData":[OSD([subQ15]),TDD([makeQuery(id+"F4.imprint","IMPRINT",EDGE,{"disambiguationData":[TD([[makeQuery(id+"F4.imprint","INTERSECT",VERTEX,{"derivedFrom":[subQ21,subQ15]}),-1.0]])],"derivedFrom":subQ15})])]})])],"derivedFrom":subQ10}),makeQuery(id+"F29.boolean.opBoolean","MERGE",FACE,{"derivedFrom":[makeQuery(id+"F5.boolean.opBoolean","SPLIT",FACE,{"disambiguationData":[TD([makeQuery(id+"F5.opExtrude","SWEPT_FACE",FACE,{"disambiguationData":[OSD([subQ15]),TDD([makeQuery(id+"F4.imprint","IMPRINT",EDGE,{"disambiguationData":[TD([[makeQuery(id+"F4.imprint","INTERSECT",VERTEX,{"derivedFrom":[subQ5,subQ15]}),1.0]])],"derivedFrom":subQ15})])]})])],"derivedFrom":subQ10}),makeQuery(id+"F7.boolean.opBoolean","MERGE",FACE,{"derivedFrom":[makeQuery(id+"F5.boolean.opBoolean","SPLIT",FACE,{"disambiguationData":[TD([makeQuery(id+"F5.opExtrude","SWEPT_FACE",FACE,{"disambiguationData":[OSD([subQ6]),TDD([makeQuery(id+"F4.imprint","IMPRINT",EDGE,{"disambiguationData":[TD([[subQ7,-1.0]])],"derivedFrom":subQ6})])]})])],"derivedFrom":subQ10}),makeQuery(id+"F7.opExtrude","SWEPT_FACE",FACE,{"disambiguationData":[OSD([sQuery(id+"F6.wireOp",EDGE,"E12")])]})]}),makeQuery(id+"F29.opExtrude","SWEPT_FACE",FACE,{"disambiguationData":[OSD([sQuery(id+"F28.wireOp",EDGE,"E57")])]})]}),makeQuery(id+"F31.opExtrude","SWEPT_FACE",FACE,{"disambiguationData":[OSD([sQuery(id+"F30.wireOp",EDGE,"E61")])]})]}),makeQuery(id+"F33.opExtrude","SWEPT_FACE",FACE,{"disambiguationData":[OSD([sQuery(id+"F32.wireOp",EDGE,"E65")])]})]}),makeQuery(id+"F35.opExtrude","SWEPT_FACE",FACE,{"disambiguationData":[OSD([sQuery(id+"F34.wireOp",EDGE,"E69")])]})]}),makeQuery(id+"F44.opExtrude","SWEPT_FACE",FACE,{"disambiguationData":[OSD([sQuery(id+"F43.wireOp",EDGE,"E87.0")])]})]}),makeQuery(id+"F46.opExtrude","SWEPT_FACE",FACE,{"disambiguationData":[OSD([sQuery(id+"F45.wireOp",EDGE,"E91")])]})]});}
            var sketch = newSketch(context, id + "F57", { "sketchPlane" : qUnion([Q0])});
            skLineSegment(sketch, "E126.bottom", {"start": v(-50.63, -101.6) * mm, "end": v(-177.63, -101.6) * mm});
            skLineSegment(sketch, "E126.top", {"start": v(-50.63, -304.8) * mm, "end": v(-177.63, -304.8) * mm});
            skLineSegment(sketch, "E126.left", {"start": v(-50.63, -101.6) * mm, "end": v(-50.63, -304.8) * mm});
            skLineSegment(sketch, "E126.right", {"start": v(-177.63, -101.6) * mm, "end": v(-177.63, -304.8) * mm});
            skPoint(sketch, "E126.middle", {"position": v(-114.13, -203.2) * mm});
            skPoint(sketch, "E126.middle.positionSnap0", {"position": v(-114.13, -346.07) * mm});
            skPoint(sketch, "E126.centerSnap0", {"position": v(-114.13, -346.07) * mm});
            skLineSegment(sketch, "E127.bottom", {"start": v(145.84, -107.95) * mm, "end": v(69.64, -107.95) * mm});
            skLineSegment(sketch, "E127.top", {"start": v(145.84, -298.45) * mm, "end": v(69.64, -298.45) * mm});
            skLineSegment(sketch, "E127.left", {"start": v(145.84, -107.95) * mm, "end": v(145.84, -298.45) * mm});
            skLineSegment(sketch, "E127.right", {"start": v(69.64, -107.95) * mm, "end": v(69.64, -298.45) * mm});
            skPoint(sketch, "E127.middle", {"position": v(107.74, -203.2) * mm});
            skPoint(sketch, "E127.cornerSnap0", {"position": v(25.4, -107.95) * mm});
            skSolve(sketch);
        }
        {
            var Q0;
            Q0 = qSketchRegion(id + "F57", true);
            extrude(context, id + "F58", {"entities" : qUnion([Q0]), "operationType" : NewBodyOperationType.ADD, "depth" : 2.54 * mm, "offsetDistance" : 25.4 * mm});
        }
        {
            var Q0;
            {var subQ2=sQuery(id+"F2.wireOp",EDGE,"E1.left");var subQ4=sQuery(id+"F4.wireOp",EDGE,"E8");var subQ5=makeQuery(id+"F3.opExtrude","CAP_EDGE",EDGE,{"disambiguationData":[OSD([subQ2])],"isStart":true});var subQ6=sQuery(id+"F4.wireOp",EDGE,"E2");var subQ7=makeQuery(id+"F4.imprint","INTERSECT",VERTEX,{"derivedFrom":[subQ6,subQ4]});var subQ10=makeQuery(id+"F1.opExtrude","CAP_FACE",FACE,{"disambiguationData":[OSD([sQuery(id+"F0.wireOp",EDGE,"E0.bottom"),sQuery(id+"F0.wireOp",EDGE,"E0.top"),sQuery(id+"F0.wireOp",EDGE,"E0.left"),sQuery(id+"F0.wireOp",EDGE,"E0.right")])],"isStart":false});var subQ15=sQuery(id+"F4.wireOp",EDGE,"E9");var subQ17=sQuery(id+"F2.wireOp",EDGE,"E1.right");var subQ19=sQuery(id+"F4.wireOp",EDGE,"E4");var subQ21=makeQuery(id+"F3.opExtrude","CAP_EDGE",EDGE,{"disambiguationData":[OSD([subQ17])],"isStart":true});var subQ22=makeQuery(id+"F4.imprint","INTERSECT",VERTEX,{"derivedFrom":[subQ19,subQ4]});Q0=makeQuery(id+"F46.boolean.opBoolean","MERGE",FACE,{"derivedFrom":[makeQuery(id+"F44.boolean.opBoolean","MERGE",FACE,{"derivedFrom":[makeQuery(id+"F35.boolean.opBoolean","MERGE",FACE,{"derivedFrom":[makeQuery(id+"F33.boolean.opBoolean","MERGE",FACE,{"derivedFrom":[makeQuery(id+"F5.boolean.opBoolean","SPLIT",FACE,{"disambiguationData":[TD([makeQuery(id+"F5.opExtrude","SWEPT_FACE",FACE,{"disambiguationData":[OSD([subQ19]),TDD([makeQuery(id+"F4.imprint","IMPRINT",EDGE,{"disambiguationData":[TD([[subQ22,-1.0]])],"derivedFrom":subQ19})])]})])],"derivedFrom":subQ10}),makeQuery(id+"F31.boolean.opBoolean","MERGE",FACE,{"derivedFrom":[makeQuery(id+"F5.boolean.opBoolean","SPLIT",FACE,{"disambiguationData":[TD([makeQuery(id+"F5.opExtrude","SWEPT_FACE",FACE,{"disambiguationData":[OSD([subQ15]),TDD([makeQuery(id+"F4.imprint","IMPRINT",EDGE,{"disambiguationData":[TD([[makeQuery(id+"F4.imprint","INTERSECT",VERTEX,{"derivedFrom":[subQ21,subQ15]}),-1.0]])],"derivedFrom":subQ15})])]})])],"derivedFrom":subQ10}),makeQuery(id+"F29.boolean.opBoolean","MERGE",FACE,{"derivedFrom":[makeQuery(id+"F5.boolean.opBoolean","SPLIT",FACE,{"disambiguationData":[TD([makeQuery(id+"F5.opExtrude","SWEPT_FACE",FACE,{"disambiguationData":[OSD([subQ15]),TDD([makeQuery(id+"F4.imprint","IMPRINT",EDGE,{"disambiguationData":[TD([[makeQuery(id+"F4.imprint","INTERSECT",VERTEX,{"derivedFrom":[subQ5,subQ15]}),1.0]])],"derivedFrom":subQ15})])]})])],"derivedFrom":subQ10}),makeQuery(id+"F7.boolean.opBoolean","MERGE",FACE,{"derivedFrom":[makeQuery(id+"F5.boolean.opBoolean","SPLIT",FACE,{"disambiguationData":[TD([makeQuery(id+"F5.opExtrude","SWEPT_FACE",FACE,{"disambiguationData":[OSD([subQ6]),TDD([makeQuery(id+"F4.imprint","IMPRINT",EDGE,{"disambiguationData":[TD([[subQ7,-1.0]])],"derivedFrom":subQ6})])]})])],"derivedFrom":subQ10}),makeQuery(id+"F7.opExtrude","SWEPT_FACE",FACE,{"disambiguationData":[OSD([sQuery(id+"F6.wireOp",EDGE,"E12")])]})]}),makeQuery(id+"F29.opExtrude","SWEPT_FACE",FACE,{"disambiguationData":[OSD([sQuery(id+"F28.wireOp",EDGE,"E57")])]})]}),makeQuery(id+"F31.opExtrude","SWEPT_FACE",FACE,{"disambiguationData":[OSD([sQuery(id+"F30.wireOp",EDGE,"E61")])]})]}),makeQuery(id+"F33.opExtrude","SWEPT_FACE",FACE,{"disambiguationData":[OSD([sQuery(id+"F32.wireOp",EDGE,"E65")])]})]}),makeQuery(id+"F35.opExtrude","SWEPT_FACE",FACE,{"disambiguationData":[OSD([sQuery(id+"F34.wireOp",EDGE,"E69")])]})]}),makeQuery(id+"F44.opExtrude","SWEPT_FACE",FACE,{"disambiguationData":[OSD([sQuery(id+"F43.wireOp",EDGE,"E87.0")])]})]}),makeQuery(id+"F46.opExtrude","SWEPT_FACE",FACE,{"disambiguationData":[OSD([sQuery(id+"F45.wireOp",EDGE,"E91")])]})]});}
            var sketch = newSketch(context, id + "F59", { "sketchPlane" : qUnion([Q0])});
            skLineSegment(sketch, "E128", {"start": v(197.42, 419.1) * mm, "end": v(197.42, 114.3) * mm});
            skLineSegment(sketch, "E129", {"start": v(197.42, 114.3) * mm, "end": v(254, 114.3) * mm});
            skLineSegment(sketch, "E130.0", {"start": v(254, 419.1) * mm, "end": v(50.8, 419.1) * mm});
            skLineSegment(sketch, "E130.1", {"start": v(254, 419.1) * mm, "end": v(254, 12.7) * mm});
            skLineSegment(sketch, "E131", {"start": v(197.42, 419.1) * mm, "end": v(254, 419.1) * mm});
            skLineSegment(sketch, "E132", {"start": v(254, 114.3) * mm, "end": v(254, 419.1) * mm});
            skSolve(sketch);
        }
        {
            var Q0;
            {var subQ2=sQuery(id+"F59.wireOp",EDGE,"E128");Q0=makeQuery(id+"F59.imprint","IMPRINT",FACE,{"disambiguationData":[TD([[makeQuery(id+"F59.imprint","IMPRINT",EDGE,{"derivedFrom":subQ2}),1.0]])]});}
            extrude(context, id + "F60", {"entities" : qUnion([Q0]), "operationType" : NewBodyOperationType.ADD, "depth" : 63.5 * mm, "offsetDistance" : 25.4 * mm});
        }
        {
            var Q0;
            {var subQ2=sQuery(id+"F2.wireOp",EDGE,"E1.left");var subQ4=sQuery(id+"F4.wireOp",EDGE,"E8");var subQ5=makeQuery(id+"F3.opExtrude","CAP_EDGE",EDGE,{"disambiguationData":[OSD([subQ2])],"isStart":true});var subQ6=sQuery(id+"F4.wireOp",EDGE,"E2");var subQ7=makeQuery(id+"F4.imprint","INTERSECT",VERTEX,{"derivedFrom":[subQ6,subQ4]});var subQ10=makeQuery(id+"F1.opExtrude","CAP_FACE",FACE,{"disambiguationData":[OSD([sQuery(id+"F0.wireOp",EDGE,"E0.bottom"),sQuery(id+"F0.wireOp",EDGE,"E0.top"),sQuery(id+"F0.wireOp",EDGE,"E0.left"),sQuery(id+"F0.wireOp",EDGE,"E0.right")])],"isStart":false});var subQ15=sQuery(id+"F4.wireOp",EDGE,"E9");var subQ17=sQuery(id+"F2.wireOp",EDGE,"E1.right");var subQ19=sQuery(id+"F4.wireOp",EDGE,"E4");var subQ21=makeQuery(id+"F3.opExtrude","CAP_EDGE",EDGE,{"disambiguationData":[OSD([subQ17])],"isStart":true});var subQ22=makeQuery(id+"F4.imprint","INTERSECT",VERTEX,{"derivedFrom":[subQ19,subQ4]});Q0=makeQuery(id+"F46.boolean.opBoolean","MERGE",FACE,{"derivedFrom":[makeQuery(id+"F44.boolean.opBoolean","MERGE",FACE,{"derivedFrom":[makeQuery(id+"F35.boolean.opBoolean","MERGE",FACE,{"derivedFrom":[makeQuery(id+"F33.boolean.opBoolean","MERGE",FACE,{"derivedFrom":[makeQuery(id+"F5.boolean.opBoolean","SPLIT",FACE,{"disambiguationData":[TD([makeQuery(id+"F5.opExtrude","SWEPT_FACE",FACE,{"disambiguationData":[OSD([subQ19]),TDD([makeQuery(id+"F4.imprint","IMPRINT",EDGE,{"disambiguationData":[TD([[subQ22,-1.0]])],"derivedFrom":subQ19})])]})])],"derivedFrom":subQ10}),makeQuery(id+"F31.boolean.opBoolean","MERGE",FACE,{"derivedFrom":[makeQuery(id+"F5.boolean.opBoolean","SPLIT",FACE,{"disambiguationData":[TD([makeQuery(id+"F5.opExtrude","SWEPT_FACE",FACE,{"disambiguationData":[OSD([subQ15]),TDD([makeQuery(id+"F4.imprint","IMPRINT",EDGE,{"disambiguationData":[TD([[makeQuery(id+"F4.imprint","INTERSECT",VERTEX,{"derivedFrom":[subQ21,subQ15]}),-1.0]])],"derivedFrom":subQ15})])]})])],"derivedFrom":subQ10}),makeQuery(id+"F29.boolean.opBoolean","MERGE",FACE,{"derivedFrom":[makeQuery(id+"F5.boolean.opBoolean","SPLIT",FACE,{"disambiguationData":[TD([makeQuery(id+"F5.opExtrude","SWEPT_FACE",FACE,{"disambiguationData":[OSD([subQ15]),TDD([makeQuery(id+"F4.imprint","IMPRINT",EDGE,{"disambiguationData":[TD([[makeQuery(id+"F4.imprint","INTERSECT",VERTEX,{"derivedFrom":[subQ5,subQ15]}),1.0]])],"derivedFrom":subQ15})])]})])],"derivedFrom":subQ10}),makeQuery(id+"F7.boolean.opBoolean","MERGE",FACE,{"derivedFrom":[makeQuery(id+"F5.boolean.opBoolean","SPLIT",FACE,{"disambiguationData":[TD([makeQuery(id+"F5.opExtrude","SWEPT_FACE",FACE,{"disambiguationData":[OSD([subQ6]),TDD([makeQuery(id+"F4.imprint","IMPRINT",EDGE,{"disambiguationData":[TD([[subQ7,-1.0]])],"derivedFrom":subQ6})])]})])],"derivedFrom":subQ10}),makeQuery(id+"F7.opExtrude","SWEPT_FACE",FACE,{"disambiguationData":[OSD([sQuery(id+"F6.wireOp",EDGE,"E12")])]})]}),makeQuery(id+"F29.opExtrude","SWEPT_FACE",FACE,{"disambiguationData":[OSD([sQuery(id+"F28.wireOp",EDGE,"E57")])]})]}),makeQuery(id+"F31.opExtrude","SWEPT_FACE",FACE,{"disambiguationData":[OSD([sQuery(id+"F30.wireOp",EDGE,"E61")])]})]}),makeQuery(id+"F33.opExtrude","SWEPT_FACE",FACE,{"disambiguationData":[OSD([sQuery(id+"F32.wireOp",EDGE,"E65")])]})]}),makeQuery(id+"F35.opExtrude","SWEPT_FACE",FACE,{"disambiguationData":[OSD([sQuery(id+"F34.wireOp",EDGE,"E69")])]})]}),makeQuery(id+"F44.opExtrude","SWEPT_FACE",FACE,{"disambiguationData":[OSD([sQuery(id+"F43.wireOp",EDGE,"E87.0")])]})]}),makeQuery(id+"F46.opExtrude","SWEPT_FACE",FACE,{"disambiguationData":[OSD([sQuery(id+"F45.wireOp",EDGE,"E91")])]})]});}
            var sketch = newSketch(context, id + "F61", { "sketchPlane" : qUnion([Q0])});
            skLineSegment(sketch, "E133", {"start": v(101.6, 419.1) * mm, "end": v(101.6, 241.3) * mm});
            skLineSegment(sketch, "E134", {"start": v(101.6, 241.3) * mm, "end": v(50.8, 241.3) * mm});
            skLineSegment(sketch, "E135", {"start": v(50.8, 241.3) * mm, "end": v(50.8, 419.1) * mm});
            skLineSegment(sketch, "E136", {"start": v(50.8, 419.1) * mm, "end": v(101.6, 419.1) * mm});
            skSolve(sketch);
        }
        {
            var Q0;
            Q0 = qSketchRegion(id + "F61", true);
            extrude(context, id + "F62", {"entities" : qUnion([Q0]), "operationType" : NewBodyOperationType.ADD, "depth" : 76.2 * mm, "offsetDistance" : 25.4 * mm});
        }
        {
            var Q0;
            {var subQ2=sQuery(id+"F2.wireOp",EDGE,"E1.left");var subQ4=sQuery(id+"F4.wireOp",EDGE,"E8");var subQ5=makeQuery(id+"F3.opExtrude","CAP_EDGE",EDGE,{"disambiguationData":[OSD([subQ2])],"isStart":true});var subQ6=sQuery(id+"F4.wireOp",EDGE,"E2");var subQ7=makeQuery(id+"F4.imprint","INTERSECT",VERTEX,{"derivedFrom":[subQ6,subQ4]});var subQ10=makeQuery(id+"F1.opExtrude","CAP_FACE",FACE,{"disambiguationData":[OSD([sQuery(id+"F0.wireOp",EDGE,"E0.bottom"),sQuery(id+"F0.wireOp",EDGE,"E0.top"),sQuery(id+"F0.wireOp",EDGE,"E0.left"),sQuery(id+"F0.wireOp",EDGE,"E0.right")])],"isStart":false});var subQ15=sQuery(id+"F4.wireOp",EDGE,"E9");var subQ17=sQuery(id+"F2.wireOp",EDGE,"E1.right");var subQ19=sQuery(id+"F4.wireOp",EDGE,"E4");var subQ21=makeQuery(id+"F3.opExtrude","CAP_EDGE",EDGE,{"disambiguationData":[OSD([subQ17])],"isStart":true});var subQ22=makeQuery(id+"F4.imprint","INTERSECT",VERTEX,{"derivedFrom":[subQ19,subQ4]});Q0=makeQuery(id+"F46.boolean.opBoolean","MERGE",FACE,{"derivedFrom":[makeQuery(id+"F44.boolean.opBoolean","MERGE",FACE,{"derivedFrom":[makeQuery(id+"F35.boolean.opBoolean","MERGE",FACE,{"derivedFrom":[makeQuery(id+"F33.boolean.opBoolean","MERGE",FACE,{"derivedFrom":[makeQuery(id+"F5.boolean.opBoolean","SPLIT",FACE,{"disambiguationData":[TD([makeQuery(id+"F5.opExtrude","SWEPT_FACE",FACE,{"disambiguationData":[OSD([subQ19]),TDD([makeQuery(id+"F4.imprint","IMPRINT",EDGE,{"disambiguationData":[TD([[subQ22,-1.0]])],"derivedFrom":subQ19})])]})])],"derivedFrom":subQ10}),makeQuery(id+"F31.boolean.opBoolean","MERGE",FACE,{"derivedFrom":[makeQuery(id+"F5.boolean.opBoolean","SPLIT",FACE,{"disambiguationData":[TD([makeQuery(id+"F5.opExtrude","SWEPT_FACE",FACE,{"disambiguationData":[OSD([subQ15]),TDD([makeQuery(id+"F4.imprint","IMPRINT",EDGE,{"disambiguationData":[TD([[makeQuery(id+"F4.imprint","INTERSECT",VERTEX,{"derivedFrom":[subQ21,subQ15]}),-1.0]])],"derivedFrom":subQ15})])]})])],"derivedFrom":subQ10}),makeQuery(id+"F29.boolean.opBoolean","MERGE",FACE,{"derivedFrom":[makeQuery(id+"F5.boolean.opBoolean","SPLIT",FACE,{"disambiguationData":[TD([makeQuery(id+"F5.opExtrude","SWEPT_FACE",FACE,{"disambiguationData":[OSD([subQ15]),TDD([makeQuery(id+"F4.imprint","IMPRINT",EDGE,{"disambiguationData":[TD([[makeQuery(id+"F4.imprint","INTERSECT",VERTEX,{"derivedFrom":[subQ5,subQ15]}),1.0]])],"derivedFrom":subQ15})])]})])],"derivedFrom":subQ10}),makeQuery(id+"F7.boolean.opBoolean","MERGE",FACE,{"derivedFrom":[makeQuery(id+"F5.boolean.opBoolean","SPLIT",FACE,{"disambiguationData":[TD([makeQuery(id+"F5.opExtrude","SWEPT_FACE",FACE,{"disambiguationData":[OSD([subQ6]),TDD([makeQuery(id+"F4.imprint","IMPRINT",EDGE,{"disambiguationData":[TD([[subQ7,-1.0]])],"derivedFrom":subQ6})])]})])],"derivedFrom":subQ10}),makeQuery(id+"F7.opExtrude","SWEPT_FACE",FACE,{"disambiguationData":[OSD([sQuery(id+"F6.wireOp",EDGE,"E12")])]})]}),makeQuery(id+"F29.opExtrude","SWEPT_FACE",FACE,{"disambiguationData":[OSD([sQuery(id+"F28.wireOp",EDGE,"E57")])]})]}),makeQuery(id+"F31.opExtrude","SWEPT_FACE",FACE,{"disambiguationData":[OSD([sQuery(id+"F30.wireOp",EDGE,"E61")])]})]}),makeQuery(id+"F33.opExtrude","SWEPT_FACE",FACE,{"disambiguationData":[OSD([sQuery(id+"F32.wireOp",EDGE,"E65")])]})]}),makeQuery(id+"F35.opExtrude","SWEPT_FACE",FACE,{"disambiguationData":[OSD([sQuery(id+"F34.wireOp",EDGE,"E69")])]})]}),makeQuery(id+"F44.opExtrude","SWEPT_FACE",FACE,{"disambiguationData":[OSD([sQuery(id+"F43.wireOp",EDGE,"E87.0")])]})]}),makeQuery(id+"F46.opExtrude","SWEPT_FACE",FACE,{"disambiguationData":[OSD([sQuery(id+"F45.wireOp",EDGE,"E91")])]})]});}
            var sketch = newSketch(context, id + "F63", { "sketchPlane" : qUnion([Q0])});
            skLineSegment(sketch, "E137.0", {"start": v(101.6, 241.3) * mm, "end": v(50.8, 241.3) * mm});
            skLineSegment(sketch, "E138", {"start": v(101.6, 241.3) * mm, "end": v(121.73, 241.3) * mm});
            skLineSegment(sketch, "E139", {"start": v(121.73, 241.3) * mm, "end": v(121.73, 175.84) * mm});
            skLineSegment(sketch, "E140", {"start": v(121.73, 175.84) * mm, "end": v(50.8, 175.84) * mm});
            skLineSegment(sketch, "E141", {"start": v(50.8, 175.84) * mm, "end": v(50.8, 241.3) * mm});
            skLineSegment(sketch, "E142", {"start": v(101.6, 175.84) * mm, "end": v(101.6, 126.06) * mm});
            skPoint(sketch, "E142.startSnap0", {"position": v(86.27, 175.84) * mm});
            skLineSegment(sketch, "E143", {"start": v(101.6, 126.06) * mm, "end": v(50.8, 126.06) * mm});
            skLineSegment(sketch, "E144", {"start": v(50.8, 126.06) * mm, "end": v(50.8, 175.84) * mm});
            skSolve(sketch);
        }
        {
            var Q0;
            Q0=makeQuery(id+"F63.imprint","IMPRINT",FACE,{"disambiguationData":[TD([[makeQuery(id+"F63.imprint","IMPRINT",EDGE,{"derivedFrom":sQuery(id+"F63.wireOp",EDGE,"E137.0")}),1.0]])]});
            extrude(context, id + "F64", {"entities" : qUnion([Q0]), "operationType" : NewBodyOperationType.ADD, "depth" : 88.9 * mm, "offsetDistance" : 25.4 * mm});
        }
        {
            var Q0;
            {var subQ2=sQuery(id+"F2.wireOp",EDGE,"E1.left");var subQ4=sQuery(id+"F4.wireOp",EDGE,"E8");var subQ5=makeQuery(id+"F3.opExtrude","CAP_EDGE",EDGE,{"disambiguationData":[OSD([subQ2])],"isStart":true});var subQ6=sQuery(id+"F4.wireOp",EDGE,"E2");var subQ7=makeQuery(id+"F4.imprint","INTERSECT",VERTEX,{"derivedFrom":[subQ6,subQ4]});var subQ10=makeQuery(id+"F1.opExtrude","CAP_FACE",FACE,{"disambiguationData":[OSD([sQuery(id+"F0.wireOp",EDGE,"E0.bottom"),sQuery(id+"F0.wireOp",EDGE,"E0.top"),sQuery(id+"F0.wireOp",EDGE,"E0.left"),sQuery(id+"F0.wireOp",EDGE,"E0.right")])],"isStart":false});var subQ15=sQuery(id+"F4.wireOp",EDGE,"E9");var subQ17=sQuery(id+"F2.wireOp",EDGE,"E1.right");var subQ19=sQuery(id+"F4.wireOp",EDGE,"E4");var subQ21=makeQuery(id+"F3.opExtrude","CAP_EDGE",EDGE,{"disambiguationData":[OSD([subQ17])],"isStart":true});var subQ22=makeQuery(id+"F4.imprint","INTERSECT",VERTEX,{"derivedFrom":[subQ19,subQ4]});Q0=makeQuery(id+"F46.boolean.opBoolean","MERGE",FACE,{"derivedFrom":[makeQuery(id+"F44.boolean.opBoolean","MERGE",FACE,{"derivedFrom":[makeQuery(id+"F35.boolean.opBoolean","MERGE",FACE,{"derivedFrom":[makeQuery(id+"F33.boolean.opBoolean","MERGE",FACE,{"derivedFrom":[makeQuery(id+"F5.boolean.opBoolean","SPLIT",FACE,{"disambiguationData":[TD([makeQuery(id+"F5.opExtrude","SWEPT_FACE",FACE,{"disambiguationData":[OSD([subQ19]),TDD([makeQuery(id+"F4.imprint","IMPRINT",EDGE,{"disambiguationData":[TD([[subQ22,-1.0]])],"derivedFrom":subQ19})])]})])],"derivedFrom":subQ10}),makeQuery(id+"F31.boolean.opBoolean","MERGE",FACE,{"derivedFrom":[makeQuery(id+"F5.boolean.opBoolean","SPLIT",FACE,{"disambiguationData":[TD([makeQuery(id+"F5.opExtrude","SWEPT_FACE",FACE,{"disambiguationData":[OSD([subQ15]),TDD([makeQuery(id+"F4.imprint","IMPRINT",EDGE,{"disambiguationData":[TD([[makeQuery(id+"F4.imprint","INTERSECT",VERTEX,{"derivedFrom":[subQ21,subQ15]}),-1.0]])],"derivedFrom":subQ15})])]})])],"derivedFrom":subQ10}),makeQuery(id+"F29.boolean.opBoolean","MERGE",FACE,{"derivedFrom":[makeQuery(id+"F5.boolean.opBoolean","SPLIT",FACE,{"disambiguationData":[TD([makeQuery(id+"F5.opExtrude","SWEPT_FACE",FACE,{"disambiguationData":[OSD([subQ15]),TDD([makeQuery(id+"F4.imprint","IMPRINT",EDGE,{"disambiguationData":[TD([[makeQuery(id+"F4.imprint","INTERSECT",VERTEX,{"derivedFrom":[subQ5,subQ15]}),1.0]])],"derivedFrom":subQ15})])]})])],"derivedFrom":subQ10}),makeQuery(id+"F7.boolean.opBoolean","MERGE",FACE,{"derivedFrom":[makeQuery(id+"F5.boolean.opBoolean","SPLIT",FACE,{"disambiguationData":[TD([makeQuery(id+"F5.opExtrude","SWEPT_FACE",FACE,{"disambiguationData":[OSD([subQ6]),TDD([makeQuery(id+"F4.imprint","IMPRINT",EDGE,{"disambiguationData":[TD([[subQ7,-1.0]])],"derivedFrom":subQ6})])]})])],"derivedFrom":subQ10}),makeQuery(id+"F7.opExtrude","SWEPT_FACE",FACE,{"disambiguationData":[OSD([sQuery(id+"F6.wireOp",EDGE,"E12")])]})]}),makeQuery(id+"F29.opExtrude","SWEPT_FACE",FACE,{"disambiguationData":[OSD([sQuery(id+"F28.wireOp",EDGE,"E57")])]})]}),makeQuery(id+"F31.opExtrude","SWEPT_FACE",FACE,{"disambiguationData":[OSD([sQuery(id+"F30.wireOp",EDGE,"E61")])]})]}),makeQuery(id+"F33.opExtrude","SWEPT_FACE",FACE,{"disambiguationData":[OSD([sQuery(id+"F32.wireOp",EDGE,"E65")])]})]}),makeQuery(id+"F35.opExtrude","SWEPT_FACE",FACE,{"disambiguationData":[OSD([sQuery(id+"F34.wireOp",EDGE,"E69")])]})]}),makeQuery(id+"F44.opExtrude","SWEPT_FACE",FACE,{"disambiguationData":[OSD([sQuery(id+"F43.wireOp",EDGE,"E87.0")])]})]}),makeQuery(id+"F46.opExtrude","SWEPT_FACE",FACE,{"disambiguationData":[OSD([sQuery(id+"F45.wireOp",EDGE,"E91")])]})]});}
            var sketch = newSketch(context, id + "F65", { "sketchPlane" : qUnion([Q0])});
            skLineSegment(sketch, "E145", {"start": v(101.6, 175.84) * mm, "end": v(101.6, 111.13) * mm});
            skLineSegment(sketch, "E146", {"start": v(101.6, 111.13) * mm, "end": v(50.8, 111.13) * mm});
            skLineSegment(sketch, "E147", {"start": v(50.8, 111.13) * mm, "end": v(50.8, 175.84) * mm});
            skLineSegment(sketch, "E148", {"start": v(50.8, 175.84) * mm, "end": v(101.6, 175.84) * mm});
            skSolve(sketch);
        }
        {
            var Q0;
            Q0 = qSketchRegion(id + "F65", true);
            extrude(context, id + "F66", {"entities" : qUnion([Q0]), "operationType" : NewBodyOperationType.ADD, "depth" : 177.8 * mm, "offsetDistance" : 25.4 * mm});
        }
        {
            var Q0;
            {var subQ2=sQuery(id+"F2.wireOp",EDGE,"E1.left");var subQ4=sQuery(id+"F4.wireOp",EDGE,"E8");var subQ5=makeQuery(id+"F3.opExtrude","CAP_EDGE",EDGE,{"disambiguationData":[OSD([subQ2])],"isStart":true});var subQ6=sQuery(id+"F4.wireOp",EDGE,"E2");var subQ7=makeQuery(id+"F4.imprint","INTERSECT",VERTEX,{"derivedFrom":[subQ6,subQ4]});var subQ10=makeQuery(id+"F1.opExtrude","CAP_FACE",FACE,{"disambiguationData":[OSD([sQuery(id+"F0.wireOp",EDGE,"E0.bottom"),sQuery(id+"F0.wireOp",EDGE,"E0.top"),sQuery(id+"F0.wireOp",EDGE,"E0.left"),sQuery(id+"F0.wireOp",EDGE,"E0.right")])],"isStart":false});var subQ15=sQuery(id+"F4.wireOp",EDGE,"E9");var subQ17=sQuery(id+"F2.wireOp",EDGE,"E1.right");var subQ19=sQuery(id+"F4.wireOp",EDGE,"E4");var subQ21=makeQuery(id+"F3.opExtrude","CAP_EDGE",EDGE,{"disambiguationData":[OSD([subQ17])],"isStart":true});var subQ22=makeQuery(id+"F4.imprint","INTERSECT",VERTEX,{"derivedFrom":[subQ19,subQ4]});Q0=makeQuery(id+"F46.boolean.opBoolean","MERGE",FACE,{"derivedFrom":[makeQuery(id+"F44.boolean.opBoolean","MERGE",FACE,{"derivedFrom":[makeQuery(id+"F35.boolean.opBoolean","MERGE",FACE,{"derivedFrom":[makeQuery(id+"F33.boolean.opBoolean","MERGE",FACE,{"derivedFrom":[makeQuery(id+"F5.boolean.opBoolean","SPLIT",FACE,{"disambiguationData":[TD([makeQuery(id+"F5.opExtrude","SWEPT_FACE",FACE,{"disambiguationData":[OSD([subQ19]),TDD([makeQuery(id+"F4.imprint","IMPRINT",EDGE,{"disambiguationData":[TD([[subQ22,-1.0]])],"derivedFrom":subQ19})])]})])],"derivedFrom":subQ10}),makeQuery(id+"F31.boolean.opBoolean","MERGE",FACE,{"derivedFrom":[makeQuery(id+"F5.boolean.opBoolean","SPLIT",FACE,{"disambiguationData":[TD([makeQuery(id+"F5.opExtrude","SWEPT_FACE",FACE,{"disambiguationData":[OSD([subQ15]),TDD([makeQuery(id+"F4.imprint","IMPRINT",EDGE,{"disambiguationData":[TD([[makeQuery(id+"F4.imprint","INTERSECT",VERTEX,{"derivedFrom":[subQ21,subQ15]}),-1.0]])],"derivedFrom":subQ15})])]})])],"derivedFrom":subQ10}),makeQuery(id+"F29.boolean.opBoolean","MERGE",FACE,{"derivedFrom":[makeQuery(id+"F5.boolean.opBoolean","SPLIT",FACE,{"disambiguationData":[TD([makeQuery(id+"F5.opExtrude","SWEPT_FACE",FACE,{"disambiguationData":[OSD([subQ15]),TDD([makeQuery(id+"F4.imprint","IMPRINT",EDGE,{"disambiguationData":[TD([[makeQuery(id+"F4.imprint","INTERSECT",VERTEX,{"derivedFrom":[subQ5,subQ15]}),1.0]])],"derivedFrom":subQ15})])]})])],"derivedFrom":subQ10}),makeQuery(id+"F7.boolean.opBoolean","MERGE",FACE,{"derivedFrom":[makeQuery(id+"F5.boolean.opBoolean","SPLIT",FACE,{"disambiguationData":[TD([makeQuery(id+"F5.opExtrude","SWEPT_FACE",FACE,{"disambiguationData":[OSD([subQ6]),TDD([makeQuery(id+"F4.imprint","IMPRINT",EDGE,{"disambiguationData":[TD([[subQ7,-1.0]])],"derivedFrom":subQ6})])]})])],"derivedFrom":subQ10}),makeQuery(id+"F7.opExtrude","SWEPT_FACE",FACE,{"disambiguationData":[OSD([sQuery(id+"F6.wireOp",EDGE,"E12")])]})]}),makeQuery(id+"F29.opExtrude","SWEPT_FACE",FACE,{"disambiguationData":[OSD([sQuery(id+"F28.wireOp",EDGE,"E57")])]})]}),makeQuery(id+"F31.opExtrude","SWEPT_FACE",FACE,{"disambiguationData":[OSD([sQuery(id+"F30.wireOp",EDGE,"E61")])]})]}),makeQuery(id+"F33.opExtrude","SWEPT_FACE",FACE,{"disambiguationData":[OSD([sQuery(id+"F32.wireOp",EDGE,"E65")])]})]}),makeQuery(id+"F35.opExtrude","SWEPT_FACE",FACE,{"disambiguationData":[OSD([sQuery(id+"F34.wireOp",EDGE,"E69")])]})]}),makeQuery(id+"F44.opExtrude","SWEPT_FACE",FACE,{"disambiguationData":[OSD([sQuery(id+"F43.wireOp",EDGE,"E87.0")])]})]}),makeQuery(id+"F46.opExtrude","SWEPT_FACE",FACE,{"disambiguationData":[OSD([sQuery(id+"F45.wireOp",EDGE,"E91")])]})]});}
            var sketch = newSketch(context, id + "F67", { "sketchPlane" : qUnion([Q0])});
            skLineSegment(sketch, "E149.bottom", {"start": v(-63.5, 317.5) * mm, "end": v(-165.1, 317.5) * mm});
            skLineSegment(sketch, "E149.top", {"start": v(-63.5, 114.3) * mm, "end": v(-165.1, 114.3) * mm});
            skLineSegment(sketch, "E149.left", {"start": v(-63.5, 317.5) * mm, "end": v(-63.5, 114.3) * mm});
            skLineSegment(sketch, "E149.right", {"start": v(-165.1, 317.5) * mm, "end": v(-165.1, 114.3) * mm});
            skPoint(sketch, "E149.middle", {"position": v(-114.3, 215.9) * mm});
            skPoint(sketch, "E149.middle.positionSnap0", {"position": v(-114.3, 419.1) * mm});
            skPoint(sketch, "E149.middle.positionSnap1", {"position": v(-254, 215.9) * mm});
            skPoint(sketch, "E149.centerSnap0", {"position": v(-114.3, 419.1) * mm});
            skPoint(sketch, "E149.centerSnap1", {"position": v(-254, 215.9) * mm});
            skSolve(sketch);
        }
        {
            var Q0;
            Q0 = qSketchRegion(id + "F67", true);
            extrude(context, id + "F68", {"entities" : qUnion([Q0]), "operationType" : NewBodyOperationType.ADD, "depth" : 88.9 * mm, "offsetDistance" : 25.4 * mm});
        }
        {
            var Q0;
            Q0=makeQuery(id+"F68.opExtrude","SWEPT_FACE",FACE,{"disambiguationData":[OSD([sQuery(id+"F67.wireOp",EDGE,"E149.top")])]});
            var sketch = newSketch(context, id + "F69", { "sketchPlane" : qUnion([Q0])});
            skLineSegment(sketch, "E150", {"start": v(-153.37, 2.54) * mm, "end": v(-153.37, 73.98) * mm});
            skLineSegment(sketch, "E151", {"start": v(-153.37, 73.98) * mm, "end": v(-73.8, 73.98) * mm});
            skLineSegment(sketch, "E152", {"start": v(-73.8, 73.98) * mm, "end": v(-73.8, 2.54) * mm});
            skLineSegment(sketch, "E153", {"start": v(-153.37, 2.54) * mm, "end": v(-73.8, 2.54) * mm});
            skSolve(sketch);
        }
        {
            var Q0;
            Q0 = qSketchRegion(id + "F69", true);
            extrude(context, id + "F70", {"entities" : qUnion([Q0]), "operationType" : NewBodyOperationType.REMOVE, "oppositeDirection" : true, "depth" : 203.2 * mm, "offsetDistance" : 25.4 * mm});
        }
        {
            var Q0;
            Q0=makeQuery(id+"F68.opExtrude","SWEPT_FACE",FACE,{"disambiguationData":[OSD([sQuery(id+"F67.wireOp",EDGE,"E149.left")])]});
            var sketch = newSketch(context, id + "F71", { "sketchPlane" : qUnion([Q0])});
            skLineSegment(sketch, "E154", {"start": v(127.7, 2.54) * mm, "end": v(127.7, 79.66) * mm});
            skLineSegment(sketch, "E155", {"start": v(127.7, 79.66) * mm, "end": v(304.88, 79.66) * mm});
            skLineSegment(sketch, "E156", {"start": v(304.88, 79.66) * mm, "end": v(304.88, 2.54) * mm});
            skLineSegment(sketch, "E157", {"start": v(304.88, 2.54) * mm, "end": v(127.7, 2.54) * mm});
            skSolve(sketch);
        }
        {
            var Q0;
            Q0 = qSketchRegion(id + "F71", true);
            extrude(context, id + "F72", {"entities" : qUnion([Q0]), "operationType" : NewBodyOperationType.REMOVE, "oppositeDirection" : true, "depth" : 101.6 * mm, "offsetDistance" : 25.4 * mm});
        }
        {
            var Q0;
            {var subQ3=sQuery(id+"F2.wireOp",EDGE,"E1.right");var subQ5=sQuery(id+"F2.wireOp",EDGE,"E1.top");Q0=makeQuery(id+"F5.boolean.opBoolean","SPLIT",FACE,{"disambiguationData":[TD([makeQuery(id+"F3.opExtrude","SWEPT_FACE",FACE,{"disambiguationData":[OSD([subQ5])]})])],"derivedFrom":makeQuery(id+"F3.opExtrude","SWEPT_FACE",FACE,{"disambiguationData":[OSD([subQ3])]})});}
            var sketch = newSketch(context, id + "F73", { "sketchPlane" : qUnion([Q0])});
            skLineSegment(sketch, "E158.bottom", {"start": v(-180.68, 219.13) * mm, "end": v(-294.98, 219.13) * mm});
            skLineSegment(sketch, "E158.top", {"start": v(-180.68, 137.85) * mm, "end": v(-294.98, 137.85) * mm});
            skLineSegment(sketch, "E158.left", {"start": v(-180.68, 219.13) * mm, "end": v(-180.68, 137.85) * mm});
            skLineSegment(sketch, "E158.right", {"start": v(-294.98, 219.13) * mm, "end": v(-294.98, 137.85) * mm});
            skPoint(sketch, "E158.middle", {"position": v(-237.83, 178.49) * mm});
            skSolve(sketch);
        }
        {
            var Q0;
            Q0 = qSketchRegion(id + "F73", true);
            extrude(context, id + "F74", {"entities" : qUnion([Q0]), "operationType" : NewBodyOperationType.ADD, "depth" : 12.7 * mm, "offsetDistance" : 25.4 * mm});
        }
        {
            var Q0;
            {var subQ2=sQuery(id+"F2.wireOp",EDGE,"E1.left");var subQ4=sQuery(id+"F4.wireOp",EDGE,"E8");var subQ5=makeQuery(id+"F3.opExtrude","CAP_EDGE",EDGE,{"disambiguationData":[OSD([subQ2])],"isStart":true});var subQ6=sQuery(id+"F4.wireOp",EDGE,"E2");var subQ7=makeQuery(id+"F4.imprint","INTERSECT",VERTEX,{"derivedFrom":[subQ6,subQ4]});var subQ10=makeQuery(id+"F1.opExtrude","CAP_FACE",FACE,{"disambiguationData":[OSD([sQuery(id+"F0.wireOp",EDGE,"E0.bottom"),sQuery(id+"F0.wireOp",EDGE,"E0.top"),sQuery(id+"F0.wireOp",EDGE,"E0.left"),sQuery(id+"F0.wireOp",EDGE,"E0.right")])],"isStart":false});var subQ15=sQuery(id+"F4.wireOp",EDGE,"E9");var subQ17=sQuery(id+"F2.wireOp",EDGE,"E1.right");var subQ19=sQuery(id+"F4.wireOp",EDGE,"E4");var subQ21=makeQuery(id+"F3.opExtrude","CAP_EDGE",EDGE,{"disambiguationData":[OSD([subQ17])],"isStart":true});var subQ22=makeQuery(id+"F4.imprint","INTERSECT",VERTEX,{"derivedFrom":[subQ19,subQ4]});Q0=makeQuery(id+"F72.boolean.opBoolean","MERGE",FACE,{"derivedFrom":[makeQuery(id+"F70.boolean.opBoolean","MERGE",FACE,{"derivedFrom":[makeQuery(id+"F46.boolean.opBoolean","MERGE",FACE,{"derivedFrom":[makeQuery(id+"F44.boolean.opBoolean","MERGE",FACE,{"derivedFrom":[makeQuery(id+"F35.boolean.opBoolean","MERGE",FACE,{"derivedFrom":[makeQuery(id+"F33.boolean.opBoolean","MERGE",FACE,{"derivedFrom":[makeQuery(id+"F5.boolean.opBoolean","SPLIT",FACE,{"disambiguationData":[TD([makeQuery(id+"F5.opExtrude","SWEPT_FACE",FACE,{"disambiguationData":[OSD([subQ19]),TDD([makeQuery(id+"F4.imprint","IMPRINT",EDGE,{"disambiguationData":[TD([[subQ22,-1.0]])],"derivedFrom":subQ19})])]})])],"derivedFrom":subQ10}),makeQuery(id+"F31.boolean.opBoolean","MERGE",FACE,{"derivedFrom":[makeQuery(id+"F5.boolean.opBoolean","SPLIT",FACE,{"disambiguationData":[TD([makeQuery(id+"F5.opExtrude","SWEPT_FACE",FACE,{"disambiguationData":[OSD([subQ15]),TDD([makeQuery(id+"F4.imprint","IMPRINT",EDGE,{"disambiguationData":[TD([[makeQuery(id+"F4.imprint","INTERSECT",VERTEX,{"derivedFrom":[subQ21,subQ15]}),-1.0]])],"derivedFrom":subQ15})])]})])],"derivedFrom":subQ10}),makeQuery(id+"F29.boolean.opBoolean","MERGE",FACE,{"derivedFrom":[makeQuery(id+"F5.boolean.opBoolean","SPLIT",FACE,{"disambiguationData":[TD([makeQuery(id+"F5.opExtrude","SWEPT_FACE",FACE,{"disambiguationData":[OSD([subQ15]),TDD([makeQuery(id+"F4.imprint","IMPRINT",EDGE,{"disambiguationData":[TD([[makeQuery(id+"F4.imprint","INTERSECT",VERTEX,{"derivedFrom":[subQ5,subQ15]}),1.0]])],"derivedFrom":subQ15})])]})])],"derivedFrom":subQ10}),makeQuery(id+"F7.boolean.opBoolean","MERGE",FACE,{"derivedFrom":[makeQuery(id+"F5.boolean.opBoolean","SPLIT",FACE,{"disambiguationData":[TD([makeQuery(id+"F5.opExtrude","SWEPT_FACE",FACE,{"disambiguationData":[OSD([subQ6]),TDD([makeQuery(id+"F4.imprint","IMPRINT",EDGE,{"disambiguationData":[TD([[subQ7,-1.0]])],"derivedFrom":subQ6})])]})])],"derivedFrom":subQ10}),makeQuery(id+"F7.opExtrude","SWEPT_FACE",FACE,{"disambiguationData":[OSD([sQuery(id+"F6.wireOp",EDGE,"E12")])]})]}),makeQuery(id+"F29.opExtrude","SWEPT_FACE",FACE,{"disambiguationData":[OSD([sQuery(id+"F28.wireOp",EDGE,"E57")])]})]}),makeQuery(id+"F31.opExtrude","SWEPT_FACE",FACE,{"disambiguationData":[OSD([sQuery(id+"F30.wireOp",EDGE,"E61")])]})]}),makeQuery(id+"F33.opExtrude","SWEPT_FACE",FACE,{"disambiguationData":[OSD([sQuery(id+"F32.wireOp",EDGE,"E65")])]})]}),makeQuery(id+"F35.opExtrude","SWEPT_FACE",FACE,{"disambiguationData":[OSD([sQuery(id+"F34.wireOp",EDGE,"E69")])]})]}),makeQuery(id+"F44.opExtrude","SWEPT_FACE",FACE,{"disambiguationData":[OSD([sQuery(id+"F43.wireOp",EDGE,"E87.0")])]})]}),makeQuery(id+"F46.opExtrude","SWEPT_FACE",FACE,{"disambiguationData":[OSD([sQuery(id+"F45.wireOp",EDGE,"E91")])]})]}),makeQuery(id+"F70.opExtrude","SWEPT_FACE",FACE,{"disambiguationData":[OSD([sQuery(id+"F69.wireOp",EDGE,"E153")])]})]}),makeQuery(id+"F72.opExtrude","SWEPT_FACE",FACE,{"disambiguationData":[OSD([sQuery(id+"F71.wireOp",EDGE,"E157")])]})]});}
            var sketch = newSketch(context, id + "F75", { "sketchPlane" : qUnion([Q0])});
            skLineSegment(sketch, "E159", {"start": v(14.68, -88.53) * mm, "end": v(-46.28, -88.53) * mm});
            skLineSegment(sketch, "E160", {"start": v(-46.28, -88.53) * mm, "end": v(-46.28, -27.57) * mm});
            skLineSegment(sketch, "E161", {"start": v(-46.28, -27.57) * mm, "end": v(14.68, -27.57) * mm});
            skLineSegment(sketch, "E162", {"start": v(14.68, -27.57) * mm, "end": v(14.68, -88.53) * mm});
            skSolve(sketch);
        }
        {
            var Q0;
            Q0 = qSketchRegion(id + "F75", true);
            extrude(context, id + "F76", {"entities" : qUnion([Q0]), "operationType" : NewBodyOperationType.ADD, "depth" : 76.2 * mm, "offsetDistance" : 25.4 * mm});
        }
        {
            var Q0;
            Q0=makeQuery(id+"F76.opExtrude","CAP_FACE",FACE,{"disambiguationData":[OSD([sQuery(id+"F75.wireOp",EDGE,"E159"),sQuery(id+"F75.wireOp",EDGE,"E160"),sQuery(id+"F75.wireOp",EDGE,"E161"),sQuery(id+"F75.wireOp",EDGE,"E162")])],"isStart":false});
            var sketch = newSketch(context, id + "F77", { "sketchPlane" : qUnion([Q0])});
            skLineSegment(sketch, "E163", {"start": v(-46.28, -36.04) * mm, "end": v(-8.18, -36.04) * mm});
            skLineSegment(sketch, "E164", {"start": v(-8.18, -36.04) * mm, "end": v(-8.18, -81.76) * mm});
            skLineSegment(sketch, "E165", {"start": v(-8.18, -81.76) * mm, "end": v(-46.28, -81.76) * mm});
            skLineSegment(sketch, "E166", {"start": v(-46.28, -81.76) * mm, "end": v(-46.28, -36.04) * mm});
            skSolve(sketch);
        }
        {
            var Q0;
            Q0 = qSketchRegion(id + "F77", true);
            extrude(context, id + "F78", {"entities" : qUnion([Q0]), "operationType" : NewBodyOperationType.REMOVE, "oppositeDirection" : true, "depth" : 50.8 * mm, "offsetDistance" : 25.4 * mm});
        }
        {
            var Q0;
            Q0=makeQuery(id+"F76.opExtrude","CAP_FACE",FACE,{"disambiguationData":[OSD([sQuery(id+"F75.wireOp",EDGE,"E159"),sQuery(id+"F75.wireOp",EDGE,"E160"),sQuery(id+"F75.wireOp",EDGE,"E161"),sQuery(id+"F75.wireOp",EDGE,"E162")])],"isStart":false});
            var sketch = newSketch(context, id + "F79", { "sketchPlane" : qUnion([Q0])});
            skLineSegment(sketch, "E167.0", {"start": v(-46.28, -27.57) * mm, "end": v(14.68, -27.57) * mm});
            skLineSegment(sketch, "E168.0", {"start": v(-46.28, -36.04) * mm, "end": v(-8.18, -36.04) * mm});
            skPoint(sketch, "E169.0", {"position": v(-46.28, -31.8) * mm});
            skLineSegment(sketch, "E170.0", {"start": v(-46.28, -36.04) * mm, "end": v(-46.28, -27.57) * mm});
            skLineSegment(sketch, "E171.0", {"start": v(-46.28, -88.53) * mm, "end": v(-46.28, -81.76) * mm});
            skLineSegment(sketch, "E172.0", {"start": v(-8.18, -81.76) * mm, "end": v(-46.28, -81.76) * mm});
            skLineSegment(sketch, "E173.0", {"start": v(14.68, -88.53) * mm, "end": v(-46.28, -88.53) * mm});
            skLineSegment(sketch, "E174", {"start": v(-8.18, -36.04) * mm, "end": v(-8.18, -27.57) * mm});
            skLineSegment(sketch, "E175", {"start": v(-8.18, -81.76) * mm, "end": v(-8.18, -88.53) * mm});
            skSolve(sketch);
        }
        {
            var Q0;
            Q0 = qSketchRegion(id + "F79", true);
            extrude(context, id + "F80", {"entities" : qUnion([Q0]), "operationType" : NewBodyOperationType.REMOVE, "oppositeDirection" : true, "depth" : 38.1 * mm, "offsetDistance" : 25.4 * mm});
        }
    });
